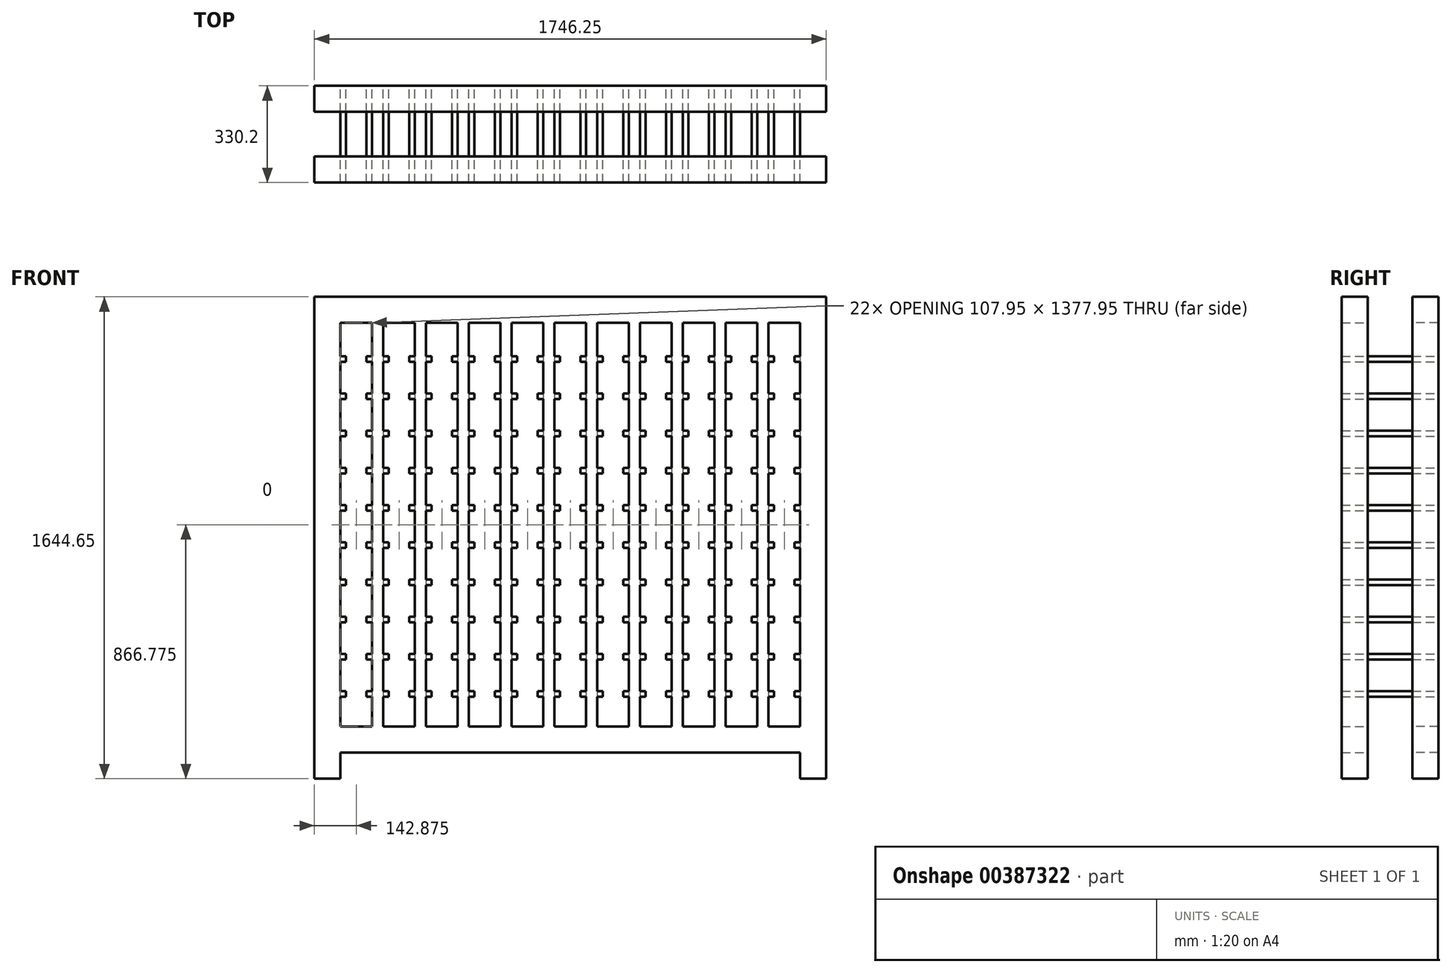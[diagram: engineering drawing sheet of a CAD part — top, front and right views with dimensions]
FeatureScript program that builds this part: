
annotation { "Feature Type Name" : "Feature", "Feature Type Description" : "" }
export const myFeature = defineFeature(function(context is Context, id is Id, definition is map)
    precondition{}
    {
        {
            var Q0;
            Q0=qCreatedBy(makeId("Front.planeOp"),FACE);
            var sketch = newSketch(context, id + "F0", { "sketchPlane" : qUnion([Q0])});
            skLineSegment(sketch, "E0.bottom", {"start": v(0, 0) * mm, "end": v(88.9, 0) * mm});
            skLineSegment(sketch, "E0.top", {"start": v(0, 1644.65) * mm, "end": v(88.9, 1644.65) * mm});
            skLineSegment(sketch, "E0.left", {"start": v(0, 0) * mm, "end": v(0, 1644.65) * mm});
            skLineSegment(sketch, "E0.right", {"start": v(88.9, 0) * mm, "end": v(88.9, 1644.65) * mm});
            skLineSegment(sketch, "E1.bottom", {"start": v(88.9, 1644.65) * mm, "end": v(1657.35, 1644.65) * mm});
            skLineSegment(sketch, "E1.top", {"start": v(88.9, 1555.75) * mm, "end": v(1657.35, 1555.75) * mm});
            skLineSegment(sketch, "E1.left", {"start": v(88.9, 1644.65) * mm, "end": v(88.9, 1555.75) * mm});
            skLineSegment(sketch, "E1.right", {"start": v(1657.35, 1644.65) * mm, "end": v(1657.35, 1555.75) * mm});
            skLineSegment(sketch, "E2.bottom", {"start": v(88.9, 177.8) * mm, "end": v(1657.35, 177.8) * mm});
            skLineSegment(sketch, "E2.top", {"start": v(88.9, 88.9) * mm, "end": v(1657.35, 88.9) * mm});
            skLineSegment(sketch, "E2.left", {"start": v(88.9, 177.8) * mm, "end": v(88.9, 88.9) * mm});
            skLineSegment(sketch, "E2.right", {"start": v(1657.35, 177.8) * mm, "end": v(1657.35, 88.9) * mm});
            skLineSegment(sketch, "E3.bottom", {"start": v(1657.35, 1644.65) * mm, "end": v(1746.25, 1644.65) * mm});
            skLineSegment(sketch, "E3.top", {"start": v(1657.35, 0) * mm, "end": v(1746.25, 0) * mm});
            skLineSegment(sketch, "E3.left", {"start": v(1657.35, 1644.65) * mm, "end": v(1657.35, 0) * mm});
            skLineSegment(sketch, "E3.right", {"start": v(1746.25, 1644.65) * mm, "end": v(1746.25, 0) * mm});
            skSolve(sketch);
        }
        {
            var Q0;
            Q0 = qSketchRegion(id + "F0", true);
            extrude(context, id + "F1", {"entities" : qUnion([Q0]), "depth" : 88.9 * mm});
        }
        {
            var Q0;
            Q0=makeQuery(id+"F1.opExtrude","CAP_FACE",FACE,{"disambiguationData":[OSD([sQuery(id+"F0.wireOp",EDGE,"E0.bottom"),sQuery(id+"F0.wireOp",EDGE,"E0.top"),sQuery(id+"F0.wireOp",EDGE,"E0.left"),sQuery(id+"F0.wireOp",EDGE,"E0.right"),sQuery(id+"F0.wireOp",EDGE,"E1.bottom"),sQuery(id+"F0.wireOp",EDGE,"E1.top"),sQuery(id+"F0.wireOp",EDGE,"E2.bottom"),sQuery(id+"F0.wireOp",EDGE,"E2.top"),sQuery(id+"F0.wireOp",EDGE,"E3.bottom"),sQuery(id+"F0.wireOp",EDGE,"E3.top"),sQuery(id+"F0.wireOp",EDGE,"E3.left"),sQuery(id+"F0.wireOp",EDGE,"E3.right")])],"isStart":false});
            var sketch = newSketch(context, id + "F2", { "sketchPlane" : qUnion([Q0])});
            skLineSegment(sketch, "E4.bottom", {"start": v(196.85, 1555.75) * mm, "end": v(234.95, 1555.75) * mm});
            skLineSegment(sketch, "E4.top", {"start": v(196.85, 177.8) * mm, "end": v(234.95, 177.8) * mm});
            skLineSegment(sketch, "E4.left", {"start": v(196.85, 1555.75) * mm, "end": v(196.85, 177.8) * mm});
            skLineSegment(sketch, "E4.right", {"start": v(234.95, 1555.75) * mm, "end": v(234.95, 177.8) * mm});
            skLineSegment(sketch, "E5.1.0.0", {"start": v(342.9, 1555.75) * mm, "end": v(342.9, 177.8) * mm});
            skLineSegment(sketch, "E5.1.0.1", {"start": v(381, 1555.75) * mm, "end": v(381, 177.8) * mm});
            skLineSegment(sketch, "E5.2.0.0", {"start": v(488.95, 1555.75) * mm, "end": v(488.95, 177.8) * mm});
            skLineSegment(sketch, "E5.2.0.1", {"start": v(527.05, 1555.75) * mm, "end": v(527.05, 177.8) * mm});
            skLineSegment(sketch, "E5.3.0.0", {"start": v(635, 1555.75) * mm, "end": v(635, 177.8) * mm});
            skLineSegment(sketch, "E5.3.0.1", {"start": v(673.1, 1555.75) * mm, "end": v(673.1, 177.8) * mm});
            skLineSegment(sketch, "E5.4.0.0", {"start": v(781.05, 1555.75) * mm, "end": v(781.05, 177.8) * mm});
            skLineSegment(sketch, "E5.4.0.1", {"start": v(819.15, 1555.75) * mm, "end": v(819.15, 177.8) * mm});
            skLineSegment(sketch, "E5.5.0.0", {"start": v(927.1, 1555.75) * mm, "end": v(927.1, 177.8) * mm});
            skLineSegment(sketch, "E5.5.0.1", {"start": v(965.2, 1555.75) * mm, "end": v(965.2, 177.8) * mm});
            skLineSegment(sketch, "E5.6.0.0", {"start": v(1073.15, 1555.75) * mm, "end": v(1073.15, 177.8) * mm});
            skLineSegment(sketch, "E5.6.0.1", {"start": v(1111.25, 1555.75) * mm, "end": v(1111.25, 177.8) * mm});
            skLineSegment(sketch, "E5.7.0.0", {"start": v(1219.2, 1555.75) * mm, "end": v(1219.2, 177.8) * mm});
            skLineSegment(sketch, "E5.7.0.1", {"start": v(1257.3, 1555.75) * mm, "end": v(1257.3, 177.8) * mm});
            skLineSegment(sketch, "E5.8.0.0", {"start": v(1365.25, 1555.75) * mm, "end": v(1365.25, 177.8) * mm});
            skLineSegment(sketch, "E5.8.0.1", {"start": v(1403.35, 1555.75) * mm, "end": v(1403.35, 177.8) * mm});
            skLineSegment(sketch, "E5.9.0.0", {"start": v(1511.3, 1555.75) * mm, "end": v(1511.3, 177.8) * mm});
            skLineSegment(sketch, "E5.9.0.1", {"start": v(1549.4, 1555.75) * mm, "end": v(1549.4, 177.8) * mm});
            skLineSegment(sketch, "E5.10.0.0", {"start": v(1657.35, 1555.75) * mm, "end": v(1657.35, 177.8) * mm});
            skLineSegment(sketch, "E5.10.0.1", {"start": v(1695.45, 1555.75) * mm, "end": v(1695.45, 177.8) * mm});
            skLineSegment(sketch, "E5.direction1", {"start": v(196.85, 177.8) * mm, "end": v(342.9, 177.8) * mm, "construction": true});
            skSolve(sketch);
        }
        {
            var Q0;
            Q0 = qSketchRegion(id + "F2", true);
            var Q1;
            {var subQ0=sQuery(id+"F2.wireOp",EDGE,"E5.1.0.0");Q1=makeQuery(id+"F2.imprint","IMPRINT",FACE,{"disambiguationData":[TD([[makeQuery(id+"F2.imprint","IMPRINT",EDGE,{"derivedFrom":subQ0}),1.0]])]});}
            var Q2;
            {var subQ0=sQuery(id+"F2.wireOp",EDGE,"E5.2.0.0");Q2=makeQuery(id+"F2.imprint","IMPRINT",FACE,{"disambiguationData":[TD([[makeQuery(id+"F2.imprint","IMPRINT",EDGE,{"derivedFrom":subQ0}),1.0]])]});}
            var Q3;
            {var subQ0=sQuery(id+"F2.wireOp",EDGE,"E5.3.0.0");Q3=makeQuery(id+"F2.imprint","IMPRINT",FACE,{"disambiguationData":[TD([[makeQuery(id+"F2.imprint","IMPRINT",EDGE,{"derivedFrom":subQ0}),1.0]])]});}
            var Q4;
            {var subQ0=sQuery(id+"F2.wireOp",EDGE,"E5.4.0.0");Q4=makeQuery(id+"F2.imprint","IMPRINT",FACE,{"disambiguationData":[TD([[makeQuery(id+"F2.imprint","IMPRINT",EDGE,{"derivedFrom":subQ0}),1.0]])]});}
            var Q5;
            {var subQ0=sQuery(id+"F2.wireOp",EDGE,"E5.5.0.0");Q5=makeQuery(id+"F2.imprint","IMPRINT",FACE,{"disambiguationData":[TD([[makeQuery(id+"F2.imprint","IMPRINT",EDGE,{"derivedFrom":subQ0}),1.0]])]});}
            var Q6;
            {var subQ0=sQuery(id+"F2.wireOp",EDGE,"E5.6.0.0");Q6=makeQuery(id+"F2.imprint","IMPRINT",FACE,{"disambiguationData":[TD([[makeQuery(id+"F2.imprint","IMPRINT",EDGE,{"derivedFrom":subQ0}),1.0]])]});}
            var Q7;
            {var subQ0=sQuery(id+"F2.wireOp",EDGE,"E5.7.0.0");Q7=makeQuery(id+"F2.imprint","IMPRINT",FACE,{"disambiguationData":[TD([[makeQuery(id+"F2.imprint","IMPRINT",EDGE,{"derivedFrom":subQ0}),1.0]])]});}
            var Q8;
            {var subQ0=sQuery(id+"F2.wireOp",EDGE,"E5.8.0.0");Q8=makeQuery(id+"F2.imprint","IMPRINT",FACE,{"disambiguationData":[TD([[makeQuery(id+"F2.imprint","IMPRINT",EDGE,{"derivedFrom":subQ0}),1.0]])]});}
            var Q9;
            {var subQ0=sQuery(id+"F2.wireOp",EDGE,"E5.9.0.0");Q9=makeQuery(id+"F2.imprint","IMPRINT",FACE,{"disambiguationData":[TD([[makeQuery(id+"F2.imprint","IMPRINT",EDGE,{"derivedFrom":subQ0}),1.0]])]});}
            var Q10;
            {var subQ0=sQuery(id+"F2.wireOp",EDGE,"E5.10.0.0");Q10=makeQuery(id+"F2.imprint","IMPRINT",FACE,{"disambiguationData":[TD([[makeQuery(id+"F2.imprint","IMPRINT",EDGE,{"derivedFrom":subQ0}),1.0]])]});}
            extrude(context, id + "F3", {"entities" : qUnion([Q0, Q1, Q2, Q3, Q4, Q5, Q6, Q7, Q8, Q9, Q10]), "operationType" : NewBodyOperationType.ADD, "oppositeDirection" : true, "depth" : 88.9 * mm});
        }
        {
            var Q0;
            {var subQ0=sQuery(id+"F0.wireOp",EDGE,"E3.right");var subQ1=sQuery(id+"F0.wireOp",EDGE,"E3.left");var subQ2=sQuery(id+"F0.wireOp",EDGE,"E3.top");var subQ3=sQuery(id+"F0.wireOp",EDGE,"E3.bottom");var subQ4=sQuery(id+"F0.wireOp",EDGE,"E2.top");var subQ5=sQuery(id+"F0.wireOp",EDGE,"E2.bottom");var subQ6=sQuery(id+"F0.wireOp",EDGE,"E1.top");var subQ7=sQuery(id+"F0.wireOp",EDGE,"E1.bottom");var subQ8=sQuery(id+"F0.wireOp",EDGE,"E0.right");var subQ9=sQuery(id+"F0.wireOp",EDGE,"E0.left");var subQ10=sQuery(id+"F0.wireOp",EDGE,"E0.top");var subQ11=sQuery(id+"F0.wireOp",EDGE,"E0.bottom");Q0=makeQuery(id+"F3.boolean.opBoolean","MERGE",FACE,{"derivedFrom":[makeQuery(id+"F1.opExtrude","CAP_FACE",FACE,{"disambiguationData":[OSD([subQ11,subQ10,subQ9,subQ8,subQ7,subQ6,subQ5,subQ4,subQ3,subQ2,subQ1,subQ0])],"isStart":false}),makeQuery(id+"F3.opExtrude","CAP_FACE",FACE,{"disambiguationData":[OSD([subQ11,subQ10,subQ9,subQ8,subQ7,subQ6,subQ5,subQ4,subQ3,subQ2,subQ1,subQ0,sQuery(id+"F2.wireOp",EDGE,"E4.left"),sQuery(id+"F2.wireOp",EDGE,"E4.right"),sQuery(id+"F2.wireOp",EDGE,"E5.1.0.0"),sQuery(id+"F2.wireOp",EDGE,"E5.1.0.1"),sQuery(id+"F2.wireOp",EDGE,"E5.2.0.0"),sQuery(id+"F2.wireOp",EDGE,"E5.2.0.1"),sQuery(id+"F2.wireOp",EDGE,"E5.3.0.0"),sQuery(id+"F2.wireOp",EDGE,"E5.3.0.1"),sQuery(id+"F2.wireOp",EDGE,"E5.4.0.0"),sQuery(id+"F2.wireOp",EDGE,"E5.4.0.1"),sQuery(id+"F2.wireOp",EDGE,"E5.5.0.0"),sQuery(id+"F2.wireOp",EDGE,"E5.5.0.1"),sQuery(id+"F2.wireOp",EDGE,"E5.6.0.0"),sQuery(id+"F2.wireOp",EDGE,"E5.6.0.1"),sQuery(id+"F2.wireOp",EDGE,"E5.7.0.0"),sQuery(id+"F2.wireOp",EDGE,"E5.7.0.1"),sQuery(id+"F2.wireOp",EDGE,"E5.8.0.0"),sQuery(id+"F2.wireOp",EDGE,"E5.8.0.1"),sQuery(id+"F2.wireOp",EDGE,"E5.9.0.0"),sQuery(id+"F2.wireOp",EDGE,"E5.9.0.1"),sQuery(id+"F2.wireOp",EDGE,"E5.10.0.0")])],"isStart":true})]});}
            cPlane(context, id + "F4", {"entities" : qUnion([Q0]), "cplaneType" : CPlaneType.OFFSET, "offset" : 165.1 * mm, "oppositeDirection" : true, "width" : 152.4 * mm, "height" : 152.4 * mm});
        }
        {
            var Q0;
            Q0=makeQuery(id+"F1.opExtrude","SWEPT_BODY",BODY,{"disambiguationData":[OSD([sQuery(id+"F0.wireOp",EDGE,"E0.bottom"),sQuery(id+"F0.wireOp",EDGE,"E0.top"),sQuery(id+"F0.wireOp",EDGE,"E0.left"),sQuery(id+"F0.wireOp",EDGE,"E0.right"),sQuery(id+"F0.wireOp",EDGE,"E1.bottom"),sQuery(id+"F0.wireOp",EDGE,"E1.top"),sQuery(id+"F0.wireOp",EDGE,"E2.bottom"),sQuery(id+"F0.wireOp",EDGE,"E2.top"),sQuery(id+"F0.wireOp",EDGE,"E3.bottom"),sQuery(id+"F0.wireOp",EDGE,"E3.top"),sQuery(id+"F0.wireOp",EDGE,"E3.left"),sQuery(id+"F0.wireOp",EDGE,"E3.right")])]});
            var Q1;
            Q1=qCreatedBy(id+"F4.planeOp",FACE);
            mirror(context, id + "F5", {"entities" : qUnion([Q0]), "mirrorPlane" : qUnion([Q1])});
        }
        {
            var Q0;
            Q0=qCreatedBy(id+"F4.planeOp",FACE);
            var sketch = newSketch(context, id + "F6", { "sketchPlane" : qUnion([Q0])});
            skLineSegment(sketch, "E6.bottom", {"start": v(88.9, 298.45) * mm, "end": v(107.95, 298.45) * mm});
            skLineSegment(sketch, "E6.top", {"start": v(88.9, 279.4) * mm, "end": v(107.95, 279.4) * mm});
            skLineSegment(sketch, "E6.left", {"start": v(88.9, 298.45) * mm, "end": v(88.9, 279.4) * mm});
            skLineSegment(sketch, "E6.right", {"start": v(107.95, 298.45) * mm, "end": v(107.95, 279.4) * mm});
            skLineSegment(sketch, "E7.0.1.0", {"start": v(107.95, 425.45) * mm, "end": v(107.95, 406.4) * mm});
            skLineSegment(sketch, "E7.0.1.1", {"start": v(88.9, 425.45) * mm, "end": v(88.9, 406.4) * mm});
            skLineSegment(sketch, "E7.0.1.2", {"start": v(88.9, 406.4) * mm, "end": v(107.95, 406.4) * mm});
            skLineSegment(sketch, "E7.0.1.3", {"start": v(88.9, 425.45) * mm, "end": v(107.95, 425.45) * mm});
            skLineSegment(sketch, "E7.0.2.0", {"start": v(107.95, 552.45) * mm, "end": v(107.95, 533.4) * mm});
            skLineSegment(sketch, "E7.0.2.1", {"start": v(88.9, 552.45) * mm, "end": v(88.9, 533.4) * mm});
            skLineSegment(sketch, "E7.0.2.2", {"start": v(88.9, 533.4) * mm, "end": v(107.95, 533.4) * mm});
            skLineSegment(sketch, "E7.0.2.3", {"start": v(88.9, 552.45) * mm, "end": v(107.95, 552.45) * mm});
            skLineSegment(sketch, "E7.0.3.0", {"start": v(107.95, 679.45) * mm, "end": v(107.95, 660.4) * mm});
            skLineSegment(sketch, "E7.0.3.1", {"start": v(88.9, 679.45) * mm, "end": v(88.9, 660.4) * mm});
            skLineSegment(sketch, "E7.0.3.2", {"start": v(88.9, 660.4) * mm, "end": v(107.95, 660.4) * mm});
            skLineSegment(sketch, "E7.0.3.3", {"start": v(88.9, 679.45) * mm, "end": v(107.95, 679.45) * mm});
            skLineSegment(sketch, "E7.0.4.0", {"start": v(107.95, 806.45) * mm, "end": v(107.95, 787.4) * mm});
            skLineSegment(sketch, "E7.0.4.1", {"start": v(88.9, 806.45) * mm, "end": v(88.9, 787.4) * mm});
            skLineSegment(sketch, "E7.0.4.2", {"start": v(88.9, 787.4) * mm, "end": v(107.95, 787.4) * mm});
            skLineSegment(sketch, "E7.0.4.3", {"start": v(88.9, 806.45) * mm, "end": v(107.95, 806.45) * mm});
            skLineSegment(sketch, "E7.0.5.0", {"start": v(107.95, 933.45) * mm, "end": v(107.95, 914.4) * mm});
            skLineSegment(sketch, "E7.0.5.1", {"start": v(88.9, 933.45) * mm, "end": v(88.9, 914.4) * mm});
            skLineSegment(sketch, "E7.0.5.2", {"start": v(88.9, 914.4) * mm, "end": v(107.95, 914.4) * mm});
            skLineSegment(sketch, "E7.0.5.3", {"start": v(88.9, 933.45) * mm, "end": v(107.95, 933.45) * mm});
            skLineSegment(sketch, "E7.0.6.0", {"start": v(107.95, 1060.45) * mm, "end": v(107.95, 1041.4) * mm});
            skLineSegment(sketch, "E7.0.6.1", {"start": v(88.9, 1060.45) * mm, "end": v(88.9, 1041.4) * mm});
            skLineSegment(sketch, "E7.0.6.2", {"start": v(88.9, 1041.4) * mm, "end": v(107.95, 1041.4) * mm});
            skLineSegment(sketch, "E7.0.6.3", {"start": v(88.9, 1060.45) * mm, "end": v(107.95, 1060.45) * mm});
            skLineSegment(sketch, "E7.0.7.0", {"start": v(107.95, 1187.45) * mm, "end": v(107.95, 1168.4) * mm});
            skLineSegment(sketch, "E7.0.7.1", {"start": v(88.9, 1187.45) * mm, "end": v(88.9, 1168.4) * mm});
            skLineSegment(sketch, "E7.0.7.2", {"start": v(88.9, 1168.4) * mm, "end": v(107.95, 1168.4) * mm});
            skLineSegment(sketch, "E7.0.7.3", {"start": v(88.9, 1187.45) * mm, "end": v(107.95, 1187.45) * mm});
            skLineSegment(sketch, "E7.0.8.0", {"start": v(107.95, 1314.45) * mm, "end": v(107.95, 1295.4) * mm});
            skLineSegment(sketch, "E7.0.8.1", {"start": v(88.9, 1314.45) * mm, "end": v(88.9, 1295.4) * mm});
            skLineSegment(sketch, "E7.0.8.2", {"start": v(88.9, 1295.4) * mm, "end": v(107.95, 1295.4) * mm});
            skLineSegment(sketch, "E7.0.8.3", {"start": v(88.9, 1314.45) * mm, "end": v(107.95, 1314.45) * mm});
            skLineSegment(sketch, "E7.1.0.0", {"start": v(254, 298.45) * mm, "end": v(254, 279.4) * mm});
            skLineSegment(sketch, "E7.1.0.1", {"start": v(234.95, 298.45) * mm, "end": v(234.95, 279.4) * mm});
            skLineSegment(sketch, "E7.1.0.2", {"start": v(234.95, 279.4) * mm, "end": v(254, 279.4) * mm});
            skLineSegment(sketch, "E7.1.0.3", {"start": v(234.95, 298.45) * mm, "end": v(254, 298.45) * mm});
            skLineSegment(sketch, "E7.1.1.0", {"start": v(254, 425.45) * mm, "end": v(254, 406.4) * mm});
            skLineSegment(sketch, "E7.1.1.1", {"start": v(234.95, 425.45) * mm, "end": v(234.95, 406.4) * mm});
            skLineSegment(sketch, "E7.1.1.2", {"start": v(234.95, 406.4) * mm, "end": v(254, 406.4) * mm});
            skLineSegment(sketch, "E7.1.1.3", {"start": v(234.95, 425.45) * mm, "end": v(254, 425.45) * mm});
            skLineSegment(sketch, "E7.1.2.0", {"start": v(254, 552.45) * mm, "end": v(254, 533.4) * mm});
            skLineSegment(sketch, "E7.1.2.1", {"start": v(234.95, 552.45) * mm, "end": v(234.95, 533.4) * mm});
            skLineSegment(sketch, "E7.1.2.2", {"start": v(234.95, 533.4) * mm, "end": v(254, 533.4) * mm});
            skLineSegment(sketch, "E7.1.2.3", {"start": v(234.95, 552.45) * mm, "end": v(254, 552.45) * mm});
            skLineSegment(sketch, "E7.1.3.0", {"start": v(254, 679.45) * mm, "end": v(254, 660.4) * mm});
            skLineSegment(sketch, "E7.1.3.1", {"start": v(234.95, 679.45) * mm, "end": v(234.95, 660.4) * mm});
            skLineSegment(sketch, "E7.1.3.2", {"start": v(234.95, 660.4) * mm, "end": v(254, 660.4) * mm});
            skLineSegment(sketch, "E7.1.3.3", {"start": v(234.95, 679.45) * mm, "end": v(254, 679.45) * mm});
            skLineSegment(sketch, "E7.1.4.0", {"start": v(254, 806.45) * mm, "end": v(254, 787.4) * mm});
            skLineSegment(sketch, "E7.1.4.1", {"start": v(234.95, 806.45) * mm, "end": v(234.95, 787.4) * mm});
            skLineSegment(sketch, "E7.1.4.2", {"start": v(234.95, 787.4) * mm, "end": v(254, 787.4) * mm});
            skLineSegment(sketch, "E7.1.4.3", {"start": v(234.95, 806.45) * mm, "end": v(254, 806.45) * mm});
            skLineSegment(sketch, "E7.1.5.0", {"start": v(254, 933.45) * mm, "end": v(254, 914.4) * mm});
            skLineSegment(sketch, "E7.1.5.1", {"start": v(234.95, 933.45) * mm, "end": v(234.95, 914.4) * mm});
            skLineSegment(sketch, "E7.1.5.2", {"start": v(234.95, 914.4) * mm, "end": v(254, 914.4) * mm});
            skLineSegment(sketch, "E7.1.5.3", {"start": v(234.95, 933.45) * mm, "end": v(254, 933.45) * mm});
            skLineSegment(sketch, "E7.1.6.0", {"start": v(254, 1060.45) * mm, "end": v(254, 1041.4) * mm});
            skLineSegment(sketch, "E7.1.6.1", {"start": v(234.95, 1060.45) * mm, "end": v(234.95, 1041.4) * mm});
            skLineSegment(sketch, "E7.1.6.2", {"start": v(234.95, 1041.4) * mm, "end": v(254, 1041.4) * mm});
            skLineSegment(sketch, "E7.1.6.3", {"start": v(234.95, 1060.45) * mm, "end": v(254, 1060.45) * mm});
            skLineSegment(sketch, "E7.1.7.0", {"start": v(254, 1187.45) * mm, "end": v(254, 1168.4) * mm});
            skLineSegment(sketch, "E7.1.7.1", {"start": v(234.95, 1187.45) * mm, "end": v(234.95, 1168.4) * mm});
            skLineSegment(sketch, "E7.1.7.2", {"start": v(234.95, 1168.4) * mm, "end": v(254, 1168.4) * mm});
            skLineSegment(sketch, "E7.1.7.3", {"start": v(234.95, 1187.45) * mm, "end": v(254, 1187.45) * mm});
            skLineSegment(sketch, "E7.1.8.0", {"start": v(254, 1314.45) * mm, "end": v(254, 1295.4) * mm});
            skLineSegment(sketch, "E7.1.8.1", {"start": v(234.95, 1314.45) * mm, "end": v(234.95, 1295.4) * mm});
            skLineSegment(sketch, "E7.1.8.2", {"start": v(234.95, 1295.4) * mm, "end": v(254, 1295.4) * mm});
            skLineSegment(sketch, "E7.1.8.3", {"start": v(234.95, 1314.45) * mm, "end": v(254, 1314.45) * mm});
            skLineSegment(sketch, "E7.2.0.0", {"start": v(400.05, 298.45) * mm, "end": v(400.05, 279.4) * mm});
            skLineSegment(sketch, "E7.2.0.1", {"start": v(381, 298.45) * mm, "end": v(381, 279.4) * mm});
            skLineSegment(sketch, "E7.2.0.2", {"start": v(381, 279.4) * mm, "end": v(400.05, 279.4) * mm});
            skLineSegment(sketch, "E7.2.0.3", {"start": v(381, 298.45) * mm, "end": v(400.05, 298.45) * mm});
            skLineSegment(sketch, "E7.2.1.0", {"start": v(400.05, 425.45) * mm, "end": v(400.05, 406.4) * mm});
            skLineSegment(sketch, "E7.2.1.1", {"start": v(381, 425.45) * mm, "end": v(381, 406.4) * mm});
            skLineSegment(sketch, "E7.2.1.2", {"start": v(381, 406.4) * mm, "end": v(400.05, 406.4) * mm});
            skLineSegment(sketch, "E7.2.1.3", {"start": v(381, 425.45) * mm, "end": v(400.05, 425.45) * mm});
            skLineSegment(sketch, "E7.2.2.0", {"start": v(400.05, 552.45) * mm, "end": v(400.05, 533.4) * mm});
            skLineSegment(sketch, "E7.2.2.1", {"start": v(381, 552.45) * mm, "end": v(381, 533.4) * mm});
            skLineSegment(sketch, "E7.2.2.2", {"start": v(381, 533.4) * mm, "end": v(400.05, 533.4) * mm});
            skLineSegment(sketch, "E7.2.2.3", {"start": v(381, 552.45) * mm, "end": v(400.05, 552.45) * mm});
            skLineSegment(sketch, "E7.2.3.0", {"start": v(400.05, 679.45) * mm, "end": v(400.05, 660.4) * mm});
            skLineSegment(sketch, "E7.2.3.1", {"start": v(381, 679.45) * mm, "end": v(381, 660.4) * mm});
            skLineSegment(sketch, "E7.2.3.2", {"start": v(381, 660.4) * mm, "end": v(400.05, 660.4) * mm});
            skLineSegment(sketch, "E7.2.3.3", {"start": v(381, 679.45) * mm, "end": v(400.05, 679.45) * mm});
            skLineSegment(sketch, "E7.2.4.0", {"start": v(400.05, 806.45) * mm, "end": v(400.05, 787.4) * mm});
            skLineSegment(sketch, "E7.2.4.1", {"start": v(381, 806.45) * mm, "end": v(381, 787.4) * mm});
            skLineSegment(sketch, "E7.2.4.2", {"start": v(381, 787.4) * mm, "end": v(400.05, 787.4) * mm});
            skLineSegment(sketch, "E7.2.4.3", {"start": v(381, 806.45) * mm, "end": v(400.05, 806.45) * mm});
            skLineSegment(sketch, "E7.2.5.0", {"start": v(400.05, 933.45) * mm, "end": v(400.05, 914.4) * mm});
            skLineSegment(sketch, "E7.2.5.1", {"start": v(381, 933.45) * mm, "end": v(381, 914.4) * mm});
            skLineSegment(sketch, "E7.2.5.2", {"start": v(381, 914.4) * mm, "end": v(400.05, 914.4) * mm});
            skLineSegment(sketch, "E7.2.5.3", {"start": v(381, 933.45) * mm, "end": v(400.05, 933.45) * mm});
            skLineSegment(sketch, "E7.2.6.0", {"start": v(400.05, 1060.45) * mm, "end": v(400.05, 1041.4) * mm});
            skLineSegment(sketch, "E7.2.6.1", {"start": v(381, 1060.45) * mm, "end": v(381, 1041.4) * mm});
            skLineSegment(sketch, "E7.2.6.2", {"start": v(381, 1041.4) * mm, "end": v(400.05, 1041.4) * mm});
            skLineSegment(sketch, "E7.2.6.3", {"start": v(381, 1060.45) * mm, "end": v(400.05, 1060.45) * mm});
            skLineSegment(sketch, "E7.2.7.0", {"start": v(400.05, 1187.45) * mm, "end": v(400.05, 1168.4) * mm});
            skLineSegment(sketch, "E7.2.7.1", {"start": v(381, 1187.45) * mm, "end": v(381, 1168.4) * mm});
            skLineSegment(sketch, "E7.2.7.2", {"start": v(381, 1168.4) * mm, "end": v(400.05, 1168.4) * mm});
            skLineSegment(sketch, "E7.2.7.3", {"start": v(381, 1187.45) * mm, "end": v(400.05, 1187.45) * mm});
            skLineSegment(sketch, "E7.2.8.0", {"start": v(400.05, 1314.45) * mm, "end": v(400.05, 1295.4) * mm});
            skLineSegment(sketch, "E7.2.8.1", {"start": v(381, 1314.45) * mm, "end": v(381, 1295.4) * mm});
            skLineSegment(sketch, "E7.2.8.2", {"start": v(381, 1295.4) * mm, "end": v(400.05, 1295.4) * mm});
            skLineSegment(sketch, "E7.2.8.3", {"start": v(381, 1314.45) * mm, "end": v(400.05, 1314.45) * mm});
            skLineSegment(sketch, "E7.3.0.0", {"start": v(546.1, 298.45) * mm, "end": v(546.1, 279.4) * mm});
            skLineSegment(sketch, "E7.3.0.1", {"start": v(527.05, 298.45) * mm, "end": v(527.05, 279.4) * mm});
            skLineSegment(sketch, "E7.3.0.2", {"start": v(527.05, 279.4) * mm, "end": v(546.1, 279.4) * mm});
            skLineSegment(sketch, "E7.3.0.3", {"start": v(527.05, 298.45) * mm, "end": v(546.1, 298.45) * mm});
            skLineSegment(sketch, "E7.3.1.0", {"start": v(546.1, 425.45) * mm, "end": v(546.1, 406.4) * mm});
            skLineSegment(sketch, "E7.3.1.1", {"start": v(527.05, 425.45) * mm, "end": v(527.05, 406.4) * mm});
            skLineSegment(sketch, "E7.3.1.2", {"start": v(527.05, 406.4) * mm, "end": v(546.1, 406.4) * mm});
            skLineSegment(sketch, "E7.3.1.3", {"start": v(527.05, 425.45) * mm, "end": v(546.1, 425.45) * mm});
            skLineSegment(sketch, "E7.3.2.0", {"start": v(546.1, 552.45) * mm, "end": v(546.1, 533.4) * mm});
            skLineSegment(sketch, "E7.3.2.1", {"start": v(527.05, 552.45) * mm, "end": v(527.05, 533.4) * mm});
            skLineSegment(sketch, "E7.3.2.2", {"start": v(527.05, 533.4) * mm, "end": v(546.1, 533.4) * mm});
            skLineSegment(sketch, "E7.3.2.3", {"start": v(527.05, 552.45) * mm, "end": v(546.1, 552.45) * mm});
            skLineSegment(sketch, "E7.3.3.0", {"start": v(546.1, 679.45) * mm, "end": v(546.1, 660.4) * mm});
            skLineSegment(sketch, "E7.3.3.1", {"start": v(527.05, 679.45) * mm, "end": v(527.05, 660.4) * mm});
            skLineSegment(sketch, "E7.3.3.2", {"start": v(527.05, 660.4) * mm, "end": v(546.1, 660.4) * mm});
            skLineSegment(sketch, "E7.3.3.3", {"start": v(527.05, 679.45) * mm, "end": v(546.1, 679.45) * mm});
            skLineSegment(sketch, "E7.3.4.0", {"start": v(546.1, 806.45) * mm, "end": v(546.1, 787.4) * mm});
            skLineSegment(sketch, "E7.3.4.1", {"start": v(527.05, 806.45) * mm, "end": v(527.05, 787.4) * mm});
            skLineSegment(sketch, "E7.3.4.2", {"start": v(527.05, 787.4) * mm, "end": v(546.1, 787.4) * mm});
            skLineSegment(sketch, "E7.3.4.3", {"start": v(527.05, 806.45) * mm, "end": v(546.1, 806.45) * mm});
            skLineSegment(sketch, "E7.3.5.0", {"start": v(546.1, 933.45) * mm, "end": v(546.1, 914.4) * mm});
            skLineSegment(sketch, "E7.3.5.1", {"start": v(527.05, 933.45) * mm, "end": v(527.05, 914.4) * mm});
            skLineSegment(sketch, "E7.3.5.2", {"start": v(527.05, 914.4) * mm, "end": v(546.1, 914.4) * mm});
            skLineSegment(sketch, "E7.3.5.3", {"start": v(527.05, 933.45) * mm, "end": v(546.1, 933.45) * mm});
            skLineSegment(sketch, "E7.3.6.0", {"start": v(546.1, 1060.45) * mm, "end": v(546.1, 1041.4) * mm});
            skLineSegment(sketch, "E7.3.6.1", {"start": v(527.05, 1060.45) * mm, "end": v(527.05, 1041.4) * mm});
            skLineSegment(sketch, "E7.3.6.2", {"start": v(527.05, 1041.4) * mm, "end": v(546.1, 1041.4) * mm});
            skLineSegment(sketch, "E7.3.6.3", {"start": v(527.05, 1060.45) * mm, "end": v(546.1, 1060.45) * mm});
            skLineSegment(sketch, "E7.3.7.0", {"start": v(546.1, 1187.45) * mm, "end": v(546.1, 1168.4) * mm});
            skLineSegment(sketch, "E7.3.7.1", {"start": v(527.05, 1187.45) * mm, "end": v(527.05, 1168.4) * mm});
            skLineSegment(sketch, "E7.3.7.2", {"start": v(527.05, 1168.4) * mm, "end": v(546.1, 1168.4) * mm});
            skLineSegment(sketch, "E7.3.7.3", {"start": v(527.05, 1187.45) * mm, "end": v(546.1, 1187.45) * mm});
            skLineSegment(sketch, "E7.3.8.0", {"start": v(546.1, 1314.45) * mm, "end": v(546.1, 1295.4) * mm});
            skLineSegment(sketch, "E7.3.8.1", {"start": v(527.05, 1314.45) * mm, "end": v(527.05, 1295.4) * mm});
            skLineSegment(sketch, "E7.3.8.2", {"start": v(527.05, 1295.4) * mm, "end": v(546.1, 1295.4) * mm});
            skLineSegment(sketch, "E7.3.8.3", {"start": v(527.05, 1314.45) * mm, "end": v(546.1, 1314.45) * mm});
            skLineSegment(sketch, "E7.4.0.0", {"start": v(692.15, 298.45) * mm, "end": v(692.15, 279.4) * mm});
            skLineSegment(sketch, "E7.4.0.1", {"start": v(673.1, 298.45) * mm, "end": v(673.1, 279.4) * mm});
            skLineSegment(sketch, "E7.4.0.2", {"start": v(673.1, 279.4) * mm, "end": v(692.15, 279.4) * mm});
            skLineSegment(sketch, "E7.4.0.3", {"start": v(673.1, 298.45) * mm, "end": v(692.15, 298.45) * mm});
            skLineSegment(sketch, "E7.4.1.0", {"start": v(692.15, 425.45) * mm, "end": v(692.15, 406.4) * mm});
            skLineSegment(sketch, "E7.4.1.1", {"start": v(673.1, 425.45) * mm, "end": v(673.1, 406.4) * mm});
            skLineSegment(sketch, "E7.4.1.2", {"start": v(673.1, 406.4) * mm, "end": v(692.15, 406.4) * mm});
            skLineSegment(sketch, "E7.4.1.3", {"start": v(673.1, 425.45) * mm, "end": v(692.15, 425.45) * mm});
            skLineSegment(sketch, "E7.4.2.0", {"start": v(692.15, 552.45) * mm, "end": v(692.15, 533.4) * mm});
            skLineSegment(sketch, "E7.4.2.1", {"start": v(673.1, 552.45) * mm, "end": v(673.1, 533.4) * mm});
            skLineSegment(sketch, "E7.4.2.2", {"start": v(673.1, 533.4) * mm, "end": v(692.15, 533.4) * mm});
            skLineSegment(sketch, "E7.4.2.3", {"start": v(673.1, 552.45) * mm, "end": v(692.15, 552.45) * mm});
            skLineSegment(sketch, "E7.4.3.0", {"start": v(692.15, 679.45) * mm, "end": v(692.15, 660.4) * mm});
            skLineSegment(sketch, "E7.4.3.1", {"start": v(673.1, 679.45) * mm, "end": v(673.1, 660.4) * mm});
            skLineSegment(sketch, "E7.4.3.2", {"start": v(673.1, 660.4) * mm, "end": v(692.15, 660.4) * mm});
            skLineSegment(sketch, "E7.4.3.3", {"start": v(673.1, 679.45) * mm, "end": v(692.15, 679.45) * mm});
            skLineSegment(sketch, "E7.4.4.0", {"start": v(692.15, 806.45) * mm, "end": v(692.15, 787.4) * mm});
            skLineSegment(sketch, "E7.4.4.1", {"start": v(673.1, 806.45) * mm, "end": v(673.1, 787.4) * mm});
            skLineSegment(sketch, "E7.4.4.2", {"start": v(673.1, 787.4) * mm, "end": v(692.15, 787.4) * mm});
            skLineSegment(sketch, "E7.4.4.3", {"start": v(673.1, 806.45) * mm, "end": v(692.15, 806.45) * mm});
            skLineSegment(sketch, "E7.4.5.0", {"start": v(692.15, 933.45) * mm, "end": v(692.15, 914.4) * mm});
            skLineSegment(sketch, "E7.4.5.1", {"start": v(673.1, 933.45) * mm, "end": v(673.1, 914.4) * mm});
            skLineSegment(sketch, "E7.4.5.2", {"start": v(673.1, 914.4) * mm, "end": v(692.15, 914.4) * mm});
            skLineSegment(sketch, "E7.4.5.3", {"start": v(673.1, 933.45) * mm, "end": v(692.15, 933.45) * mm});
            skLineSegment(sketch, "E7.4.6.0", {"start": v(692.15, 1060.45) * mm, "end": v(692.15, 1041.4) * mm});
            skLineSegment(sketch, "E7.4.6.1", {"start": v(673.1, 1060.45) * mm, "end": v(673.1, 1041.4) * mm});
            skLineSegment(sketch, "E7.4.6.2", {"start": v(673.1, 1041.4) * mm, "end": v(692.15, 1041.4) * mm});
            skLineSegment(sketch, "E7.4.6.3", {"start": v(673.1, 1060.45) * mm, "end": v(692.15, 1060.45) * mm});
            skLineSegment(sketch, "E7.4.7.0", {"start": v(692.15, 1187.45) * mm, "end": v(692.15, 1168.4) * mm});
            skLineSegment(sketch, "E7.4.7.1", {"start": v(673.1, 1187.45) * mm, "end": v(673.1, 1168.4) * mm});
            skLineSegment(sketch, "E7.4.7.2", {"start": v(673.1, 1168.4) * mm, "end": v(692.15, 1168.4) * mm});
            skLineSegment(sketch, "E7.4.7.3", {"start": v(673.1, 1187.45) * mm, "end": v(692.15, 1187.45) * mm});
            skLineSegment(sketch, "E7.4.8.0", {"start": v(692.15, 1314.45) * mm, "end": v(692.15, 1295.4) * mm});
            skLineSegment(sketch, "E7.4.8.1", {"start": v(673.1, 1314.45) * mm, "end": v(673.1, 1295.4) * mm});
            skLineSegment(sketch, "E7.4.8.2", {"start": v(673.1, 1295.4) * mm, "end": v(692.15, 1295.4) * mm});
            skLineSegment(sketch, "E7.4.8.3", {"start": v(673.1, 1314.45) * mm, "end": v(692.15, 1314.45) * mm});
            skLineSegment(sketch, "E7.5.0.0", {"start": v(838.2, 298.45) * mm, "end": v(838.2, 279.4) * mm});
            skLineSegment(sketch, "E7.5.0.1", {"start": v(819.15, 298.45) * mm, "end": v(819.15, 279.4) * mm});
            skLineSegment(sketch, "E7.5.0.2", {"start": v(819.15, 279.4) * mm, "end": v(838.2, 279.4) * mm});
            skLineSegment(sketch, "E7.5.0.3", {"start": v(819.15, 298.45) * mm, "end": v(838.2, 298.45) * mm});
            skLineSegment(sketch, "E7.5.1.0", {"start": v(838.2, 425.45) * mm, "end": v(838.2, 406.4) * mm});
            skLineSegment(sketch, "E7.5.1.1", {"start": v(819.15, 425.45) * mm, "end": v(819.15, 406.4) * mm});
            skLineSegment(sketch, "E7.5.1.2", {"start": v(819.15, 406.4) * mm, "end": v(838.2, 406.4) * mm});
            skLineSegment(sketch, "E7.5.1.3", {"start": v(819.15, 425.45) * mm, "end": v(838.2, 425.45) * mm});
            skLineSegment(sketch, "E7.5.2.0", {"start": v(838.2, 552.45) * mm, "end": v(838.2, 533.4) * mm});
            skLineSegment(sketch, "E7.5.2.1", {"start": v(819.15, 552.45) * mm, "end": v(819.15, 533.4) * mm});
            skLineSegment(sketch, "E7.5.2.2", {"start": v(819.15, 533.4) * mm, "end": v(838.2, 533.4) * mm});
            skLineSegment(sketch, "E7.5.2.3", {"start": v(819.15, 552.45) * mm, "end": v(838.2, 552.45) * mm});
            skLineSegment(sketch, "E7.5.3.0", {"start": v(838.2, 679.45) * mm, "end": v(838.2, 660.4) * mm});
            skLineSegment(sketch, "E7.5.3.1", {"start": v(819.15, 679.45) * mm, "end": v(819.15, 660.4) * mm});
            skLineSegment(sketch, "E7.5.3.2", {"start": v(819.15, 660.4) * mm, "end": v(838.2, 660.4) * mm});
            skLineSegment(sketch, "E7.5.3.3", {"start": v(819.15, 679.45) * mm, "end": v(838.2, 679.45) * mm});
            skLineSegment(sketch, "E7.5.4.0", {"start": v(838.2, 806.45) * mm, "end": v(838.2, 787.4) * mm});
            skLineSegment(sketch, "E7.5.4.1", {"start": v(819.15, 806.45) * mm, "end": v(819.15, 787.4) * mm});
            skLineSegment(sketch, "E7.5.4.2", {"start": v(819.15, 787.4) * mm, "end": v(838.2, 787.4) * mm});
            skLineSegment(sketch, "E7.5.4.3", {"start": v(819.15, 806.45) * mm, "end": v(838.2, 806.45) * mm});
            skLineSegment(sketch, "E7.5.5.0", {"start": v(838.2, 933.45) * mm, "end": v(838.2, 914.4) * mm});
            skLineSegment(sketch, "E7.5.5.1", {"start": v(819.15, 933.45) * mm, "end": v(819.15, 914.4) * mm});
            skLineSegment(sketch, "E7.5.5.2", {"start": v(819.15, 914.4) * mm, "end": v(838.2, 914.4) * mm});
            skLineSegment(sketch, "E7.5.5.3", {"start": v(819.15, 933.45) * mm, "end": v(838.2, 933.45) * mm});
            skLineSegment(sketch, "E7.5.6.0", {"start": v(838.2, 1060.45) * mm, "end": v(838.2, 1041.4) * mm});
            skLineSegment(sketch, "E7.5.6.1", {"start": v(819.15, 1060.45) * mm, "end": v(819.15, 1041.4) * mm});
            skLineSegment(sketch, "E7.5.6.2", {"start": v(819.15, 1041.4) * mm, "end": v(838.2, 1041.4) * mm});
            skLineSegment(sketch, "E7.5.6.3", {"start": v(819.15, 1060.45) * mm, "end": v(838.2, 1060.45) * mm});
            skLineSegment(sketch, "E7.5.7.0", {"start": v(838.2, 1187.45) * mm, "end": v(838.2, 1168.4) * mm});
            skLineSegment(sketch, "E7.5.7.1", {"start": v(819.15, 1187.45) * mm, "end": v(819.15, 1168.4) * mm});
            skLineSegment(sketch, "E7.5.7.2", {"start": v(819.15, 1168.4) * mm, "end": v(838.2, 1168.4) * mm});
            skLineSegment(sketch, "E7.5.7.3", {"start": v(819.15, 1187.45) * mm, "end": v(838.2, 1187.45) * mm});
            skLineSegment(sketch, "E7.5.8.0", {"start": v(838.2, 1314.45) * mm, "end": v(838.2, 1295.4) * mm});
            skLineSegment(sketch, "E7.5.8.1", {"start": v(819.15, 1314.45) * mm, "end": v(819.15, 1295.4) * mm});
            skLineSegment(sketch, "E7.5.8.2", {"start": v(819.15, 1295.4) * mm, "end": v(838.2, 1295.4) * mm});
            skLineSegment(sketch, "E7.5.8.3", {"start": v(819.15, 1314.45) * mm, "end": v(838.2, 1314.45) * mm});
            skLineSegment(sketch, "E7.6.0.0", {"start": v(984.25, 298.45) * mm, "end": v(984.25, 279.4) * mm});
            skLineSegment(sketch, "E7.6.0.1", {"start": v(965.2, 298.45) * mm, "end": v(965.2, 279.4) * mm});
            skLineSegment(sketch, "E7.6.0.2", {"start": v(965.2, 279.4) * mm, "end": v(984.25, 279.4) * mm});
            skLineSegment(sketch, "E7.6.0.3", {"start": v(965.2, 298.45) * mm, "end": v(984.25, 298.45) * mm});
            skLineSegment(sketch, "E7.6.1.0", {"start": v(984.25, 425.45) * mm, "end": v(984.25, 406.4) * mm});
            skLineSegment(sketch, "E7.6.1.1", {"start": v(965.2, 425.45) * mm, "end": v(965.2, 406.4) * mm});
            skLineSegment(sketch, "E7.6.1.2", {"start": v(965.2, 406.4) * mm, "end": v(984.25, 406.4) * mm});
            skLineSegment(sketch, "E7.6.1.3", {"start": v(965.2, 425.45) * mm, "end": v(984.25, 425.45) * mm});
            skLineSegment(sketch, "E7.6.2.0", {"start": v(984.25, 552.45) * mm, "end": v(984.25, 533.4) * mm});
            skLineSegment(sketch, "E7.6.2.1", {"start": v(965.2, 552.45) * mm, "end": v(965.2, 533.4) * mm});
            skLineSegment(sketch, "E7.6.2.2", {"start": v(965.2, 533.4) * mm, "end": v(984.25, 533.4) * mm});
            skLineSegment(sketch, "E7.6.2.3", {"start": v(965.2, 552.45) * mm, "end": v(984.25, 552.45) * mm});
            skLineSegment(sketch, "E7.6.3.0", {"start": v(984.25, 679.45) * mm, "end": v(984.25, 660.4) * mm});
            skLineSegment(sketch, "E7.6.3.1", {"start": v(965.2, 679.45) * mm, "end": v(965.2, 660.4) * mm});
            skLineSegment(sketch, "E7.6.3.2", {"start": v(965.2, 660.4) * mm, "end": v(984.25, 660.4) * mm});
            skLineSegment(sketch, "E7.6.3.3", {"start": v(965.2, 679.45) * mm, "end": v(984.25, 679.45) * mm});
            skLineSegment(sketch, "E7.6.4.0", {"start": v(984.25, 806.45) * mm, "end": v(984.25, 787.4) * mm});
            skLineSegment(sketch, "E7.6.4.1", {"start": v(965.2, 806.45) * mm, "end": v(965.2, 787.4) * mm});
            skLineSegment(sketch, "E7.6.4.2", {"start": v(965.2, 787.4) * mm, "end": v(984.25, 787.4) * mm});
            skLineSegment(sketch, "E7.6.4.3", {"start": v(965.2, 806.45) * mm, "end": v(984.25, 806.45) * mm});
            skLineSegment(sketch, "E7.6.5.0", {"start": v(984.25, 933.45) * mm, "end": v(984.25, 914.4) * mm});
            skLineSegment(sketch, "E7.6.5.1", {"start": v(965.2, 933.45) * mm, "end": v(965.2, 914.4) * mm});
            skLineSegment(sketch, "E7.6.5.2", {"start": v(965.2, 914.4) * mm, "end": v(984.25, 914.4) * mm});
            skLineSegment(sketch, "E7.6.5.3", {"start": v(965.2, 933.45) * mm, "end": v(984.25, 933.45) * mm});
            skLineSegment(sketch, "E7.6.6.0", {"start": v(984.25, 1060.45) * mm, "end": v(984.25, 1041.4) * mm});
            skLineSegment(sketch, "E7.6.6.1", {"start": v(965.2, 1060.45) * mm, "end": v(965.2, 1041.4) * mm});
            skLineSegment(sketch, "E7.6.6.2", {"start": v(965.2, 1041.4) * mm, "end": v(984.25, 1041.4) * mm});
            skLineSegment(sketch, "E7.6.6.3", {"start": v(965.2, 1060.45) * mm, "end": v(984.25, 1060.45) * mm});
            skLineSegment(sketch, "E7.6.7.0", {"start": v(984.25, 1187.45) * mm, "end": v(984.25, 1168.4) * mm});
            skLineSegment(sketch, "E7.6.7.1", {"start": v(965.2, 1187.45) * mm, "end": v(965.2, 1168.4) * mm});
            skLineSegment(sketch, "E7.6.7.2", {"start": v(965.2, 1168.4) * mm, "end": v(984.25, 1168.4) * mm});
            skLineSegment(sketch, "E7.6.7.3", {"start": v(965.2, 1187.45) * mm, "end": v(984.25, 1187.45) * mm});
            skLineSegment(sketch, "E7.6.8.0", {"start": v(984.25, 1314.45) * mm, "end": v(984.25, 1295.4) * mm});
            skLineSegment(sketch, "E7.6.8.1", {"start": v(965.2, 1314.45) * mm, "end": v(965.2, 1295.4) * mm});
            skLineSegment(sketch, "E7.6.8.2", {"start": v(965.2, 1295.4) * mm, "end": v(984.25, 1295.4) * mm});
            skLineSegment(sketch, "E7.6.8.3", {"start": v(965.2, 1314.45) * mm, "end": v(984.25, 1314.45) * mm});
            skLineSegment(sketch, "E7.7.0.0", {"start": v(1130.3, 298.45) * mm, "end": v(1130.3, 279.4) * mm});
            skLineSegment(sketch, "E7.7.0.1", {"start": v(1111.25, 298.45) * mm, "end": v(1111.25, 279.4) * mm});
            skLineSegment(sketch, "E7.7.0.2", {"start": v(1111.25, 279.4) * mm, "end": v(1130.3, 279.4) * mm});
            skLineSegment(sketch, "E7.7.0.3", {"start": v(1111.25, 298.45) * mm, "end": v(1130.3, 298.45) * mm});
            skLineSegment(sketch, "E7.7.1.0", {"start": v(1130.3, 425.45) * mm, "end": v(1130.3, 406.4) * mm});
            skLineSegment(sketch, "E7.7.1.1", {"start": v(1111.25, 425.45) * mm, "end": v(1111.25, 406.4) * mm});
            skLineSegment(sketch, "E7.7.1.2", {"start": v(1111.25, 406.4) * mm, "end": v(1130.3, 406.4) * mm});
            skLineSegment(sketch, "E7.7.1.3", {"start": v(1111.25, 425.45) * mm, "end": v(1130.3, 425.45) * mm});
            skLineSegment(sketch, "E7.7.2.0", {"start": v(1130.3, 552.45) * mm, "end": v(1130.3, 533.4) * mm});
            skLineSegment(sketch, "E7.7.2.1", {"start": v(1111.25, 552.45) * mm, "end": v(1111.25, 533.4) * mm});
            skLineSegment(sketch, "E7.7.2.2", {"start": v(1111.25, 533.4) * mm, "end": v(1130.3, 533.4) * mm});
            skLineSegment(sketch, "E7.7.2.3", {"start": v(1111.25, 552.45) * mm, "end": v(1130.3, 552.45) * mm});
            skLineSegment(sketch, "E7.7.3.0", {"start": v(1130.3, 679.45) * mm, "end": v(1130.3, 660.4) * mm});
            skLineSegment(sketch, "E7.7.3.1", {"start": v(1111.25, 679.45) * mm, "end": v(1111.25, 660.4) * mm});
            skLineSegment(sketch, "E7.7.3.2", {"start": v(1111.25, 660.4) * mm, "end": v(1130.3, 660.4) * mm});
            skLineSegment(sketch, "E7.7.3.3", {"start": v(1111.25, 679.45) * mm, "end": v(1130.3, 679.45) * mm});
            skLineSegment(sketch, "E7.7.4.0", {"start": v(1130.3, 806.45) * mm, "end": v(1130.3, 787.4) * mm});
            skLineSegment(sketch, "E7.7.4.1", {"start": v(1111.25, 806.45) * mm, "end": v(1111.25, 787.4) * mm});
            skLineSegment(sketch, "E7.7.4.2", {"start": v(1111.25, 787.4) * mm, "end": v(1130.3, 787.4) * mm});
            skLineSegment(sketch, "E7.7.4.3", {"start": v(1111.25, 806.45) * mm, "end": v(1130.3, 806.45) * mm});
            skLineSegment(sketch, "E7.7.5.0", {"start": v(1130.3, 933.45) * mm, "end": v(1130.3, 914.4) * mm});
            skLineSegment(sketch, "E7.7.5.1", {"start": v(1111.25, 933.45) * mm, "end": v(1111.25, 914.4) * mm});
            skLineSegment(sketch, "E7.7.5.2", {"start": v(1111.25, 914.4) * mm, "end": v(1130.3, 914.4) * mm});
            skLineSegment(sketch, "E7.7.5.3", {"start": v(1111.25, 933.45) * mm, "end": v(1130.3, 933.45) * mm});
            skLineSegment(sketch, "E7.7.6.0", {"start": v(1130.3, 1060.45) * mm, "end": v(1130.3, 1041.4) * mm});
            skLineSegment(sketch, "E7.7.6.1", {"start": v(1111.25, 1060.45) * mm, "end": v(1111.25, 1041.4) * mm});
            skLineSegment(sketch, "E7.7.6.2", {"start": v(1111.25, 1041.4) * mm, "end": v(1130.3, 1041.4) * mm});
            skLineSegment(sketch, "E7.7.6.3", {"start": v(1111.25, 1060.45) * mm, "end": v(1130.3, 1060.45) * mm});
            skLineSegment(sketch, "E7.7.7.0", {"start": v(1130.3, 1187.45) * mm, "end": v(1130.3, 1168.4) * mm});
            skLineSegment(sketch, "E7.7.7.1", {"start": v(1111.25, 1187.45) * mm, "end": v(1111.25, 1168.4) * mm});
            skLineSegment(sketch, "E7.7.7.2", {"start": v(1111.25, 1168.4) * mm, "end": v(1130.3, 1168.4) * mm});
            skLineSegment(sketch, "E7.7.7.3", {"start": v(1111.25, 1187.45) * mm, "end": v(1130.3, 1187.45) * mm});
            skLineSegment(sketch, "E7.7.8.0", {"start": v(1130.3, 1314.45) * mm, "end": v(1130.3, 1295.4) * mm});
            skLineSegment(sketch, "E7.7.8.1", {"start": v(1111.25, 1314.45) * mm, "end": v(1111.25, 1295.4) * mm});
            skLineSegment(sketch, "E7.7.8.2", {"start": v(1111.25, 1295.4) * mm, "end": v(1130.3, 1295.4) * mm});
            skLineSegment(sketch, "E7.7.8.3", {"start": v(1111.25, 1314.45) * mm, "end": v(1130.3, 1314.45) * mm});
            skLineSegment(sketch, "E7.8.0.0", {"start": v(1276.35, 298.45) * mm, "end": v(1276.35, 279.4) * mm});
            skLineSegment(sketch, "E7.8.0.1", {"start": v(1257.3, 298.45) * mm, "end": v(1257.3, 279.4) * mm});
            skLineSegment(sketch, "E7.8.0.2", {"start": v(1257.3, 279.4) * mm, "end": v(1276.35, 279.4) * mm});
            skLineSegment(sketch, "E7.8.0.3", {"start": v(1257.3, 298.45) * mm, "end": v(1276.35, 298.45) * mm});
            skLineSegment(sketch, "E7.8.1.0", {"start": v(1276.35, 425.45) * mm, "end": v(1276.35, 406.4) * mm});
            skLineSegment(sketch, "E7.8.1.1", {"start": v(1257.3, 425.45) * mm, "end": v(1257.3, 406.4) * mm});
            skLineSegment(sketch, "E7.8.1.2", {"start": v(1257.3, 406.4) * mm, "end": v(1276.35, 406.4) * mm});
            skLineSegment(sketch, "E7.8.1.3", {"start": v(1257.3, 425.45) * mm, "end": v(1276.35, 425.45) * mm});
            skLineSegment(sketch, "E7.8.2.0", {"start": v(1276.35, 552.45) * mm, "end": v(1276.35, 533.4) * mm});
            skLineSegment(sketch, "E7.8.2.1", {"start": v(1257.3, 552.45) * mm, "end": v(1257.3, 533.4) * mm});
            skLineSegment(sketch, "E7.8.2.2", {"start": v(1257.3, 533.4) * mm, "end": v(1276.35, 533.4) * mm});
            skLineSegment(sketch, "E7.8.2.3", {"start": v(1257.3, 552.45) * mm, "end": v(1276.35, 552.45) * mm});
            skLineSegment(sketch, "E7.8.3.0", {"start": v(1276.35, 679.45) * mm, "end": v(1276.35, 660.4) * mm});
            skLineSegment(sketch, "E7.8.3.1", {"start": v(1257.3, 679.45) * mm, "end": v(1257.3, 660.4) * mm});
            skLineSegment(sketch, "E7.8.3.2", {"start": v(1257.3, 660.4) * mm, "end": v(1276.35, 660.4) * mm});
            skLineSegment(sketch, "E7.8.3.3", {"start": v(1257.3, 679.45) * mm, "end": v(1276.35, 679.45) * mm});
            skLineSegment(sketch, "E7.8.4.0", {"start": v(1276.35, 806.45) * mm, "end": v(1276.35, 787.4) * mm});
            skLineSegment(sketch, "E7.8.4.1", {"start": v(1257.3, 806.45) * mm, "end": v(1257.3, 787.4) * mm});
            skLineSegment(sketch, "E7.8.4.2", {"start": v(1257.3, 787.4) * mm, "end": v(1276.35, 787.4) * mm});
            skLineSegment(sketch, "E7.8.4.3", {"start": v(1257.3, 806.45) * mm, "end": v(1276.35, 806.45) * mm});
            skLineSegment(sketch, "E7.8.5.0", {"start": v(1276.35, 933.45) * mm, "end": v(1276.35, 914.4) * mm});
            skLineSegment(sketch, "E7.8.5.1", {"start": v(1257.3, 933.45) * mm, "end": v(1257.3, 914.4) * mm});
            skLineSegment(sketch, "E7.8.5.2", {"start": v(1257.3, 914.4) * mm, "end": v(1276.35, 914.4) * mm});
            skLineSegment(sketch, "E7.8.5.3", {"start": v(1257.3, 933.45) * mm, "end": v(1276.35, 933.45) * mm});
            skLineSegment(sketch, "E7.8.6.0", {"start": v(1276.35, 1060.45) * mm, "end": v(1276.35, 1041.4) * mm});
            skLineSegment(sketch, "E7.8.6.1", {"start": v(1257.3, 1060.45) * mm, "end": v(1257.3, 1041.4) * mm});
            skLineSegment(sketch, "E7.8.6.2", {"start": v(1257.3, 1041.4) * mm, "end": v(1276.35, 1041.4) * mm});
            skLineSegment(sketch, "E7.8.6.3", {"start": v(1257.3, 1060.45) * mm, "end": v(1276.35, 1060.45) * mm});
            skLineSegment(sketch, "E7.8.7.0", {"start": v(1276.35, 1187.45) * mm, "end": v(1276.35, 1168.4) * mm});
            skLineSegment(sketch, "E7.8.7.1", {"start": v(1257.3, 1187.45) * mm, "end": v(1257.3, 1168.4) * mm});
            skLineSegment(sketch, "E7.8.7.2", {"start": v(1257.3, 1168.4) * mm, "end": v(1276.35, 1168.4) * mm});
            skLineSegment(sketch, "E7.8.7.3", {"start": v(1257.3, 1187.45) * mm, "end": v(1276.35, 1187.45) * mm});
            skLineSegment(sketch, "E7.8.8.0", {"start": v(1276.35, 1314.45) * mm, "end": v(1276.35, 1295.4) * mm});
            skLineSegment(sketch, "E7.8.8.1", {"start": v(1257.3, 1314.45) * mm, "end": v(1257.3, 1295.4) * mm});
            skLineSegment(sketch, "E7.8.8.2", {"start": v(1257.3, 1295.4) * mm, "end": v(1276.35, 1295.4) * mm});
            skLineSegment(sketch, "E7.8.8.3", {"start": v(1257.3, 1314.45) * mm, "end": v(1276.35, 1314.45) * mm});
            skLineSegment(sketch, "E7.9.0.0", {"start": v(1422.4, 298.45) * mm, "end": v(1422.4, 279.4) * mm});
            skLineSegment(sketch, "E7.9.0.1", {"start": v(1403.35, 298.45) * mm, "end": v(1403.35, 279.4) * mm});
            skLineSegment(sketch, "E7.9.0.2", {"start": v(1403.35, 279.4) * mm, "end": v(1422.4, 279.4) * mm});
            skLineSegment(sketch, "E7.9.0.3", {"start": v(1403.35, 298.45) * mm, "end": v(1422.4, 298.45) * mm});
            skLineSegment(sketch, "E7.9.1.0", {"start": v(1422.4, 425.45) * mm, "end": v(1422.4, 406.4) * mm});
            skLineSegment(sketch, "E7.9.1.1", {"start": v(1403.35, 425.45) * mm, "end": v(1403.35, 406.4) * mm});
            skLineSegment(sketch, "E7.9.1.2", {"start": v(1403.35, 406.4) * mm, "end": v(1422.4, 406.4) * mm});
            skLineSegment(sketch, "E7.9.1.3", {"start": v(1403.35, 425.45) * mm, "end": v(1422.4, 425.45) * mm});
            skLineSegment(sketch, "E7.9.2.0", {"start": v(1422.4, 552.45) * mm, "end": v(1422.4, 533.4) * mm});
            skLineSegment(sketch, "E7.9.2.1", {"start": v(1403.35, 552.45) * mm, "end": v(1403.35, 533.4) * mm});
            skLineSegment(sketch, "E7.9.2.2", {"start": v(1403.35, 533.4) * mm, "end": v(1422.4, 533.4) * mm});
            skLineSegment(sketch, "E7.9.2.3", {"start": v(1403.35, 552.45) * mm, "end": v(1422.4, 552.45) * mm});
            skLineSegment(sketch, "E7.9.3.0", {"start": v(1422.4, 679.45) * mm, "end": v(1422.4, 660.4) * mm});
            skLineSegment(sketch, "E7.9.3.1", {"start": v(1403.35, 679.45) * mm, "end": v(1403.35, 660.4) * mm});
            skLineSegment(sketch, "E7.9.3.2", {"start": v(1403.35, 660.4) * mm, "end": v(1422.4, 660.4) * mm});
            skLineSegment(sketch, "E7.9.3.3", {"start": v(1403.35, 679.45) * mm, "end": v(1422.4, 679.45) * mm});
            skLineSegment(sketch, "E7.9.4.0", {"start": v(1422.4, 806.45) * mm, "end": v(1422.4, 787.4) * mm});
            skLineSegment(sketch, "E7.9.4.1", {"start": v(1403.35, 806.45) * mm, "end": v(1403.35, 787.4) * mm});
            skLineSegment(sketch, "E7.9.4.2", {"start": v(1403.35, 787.4) * mm, "end": v(1422.4, 787.4) * mm});
            skLineSegment(sketch, "E7.9.4.3", {"start": v(1403.35, 806.45) * mm, "end": v(1422.4, 806.45) * mm});
            skLineSegment(sketch, "E7.9.5.0", {"start": v(1422.4, 933.45) * mm, "end": v(1422.4, 914.4) * mm});
            skLineSegment(sketch, "E7.9.5.1", {"start": v(1403.35, 933.45) * mm, "end": v(1403.35, 914.4) * mm});
            skLineSegment(sketch, "E7.9.5.2", {"start": v(1403.35, 914.4) * mm, "end": v(1422.4, 914.4) * mm});
            skLineSegment(sketch, "E7.9.5.3", {"start": v(1403.35, 933.45) * mm, "end": v(1422.4, 933.45) * mm});
            skLineSegment(sketch, "E7.9.6.0", {"start": v(1422.4, 1060.45) * mm, "end": v(1422.4, 1041.4) * mm});
            skLineSegment(sketch, "E7.9.6.1", {"start": v(1403.35, 1060.45) * mm, "end": v(1403.35, 1041.4) * mm});
            skLineSegment(sketch, "E7.9.6.2", {"start": v(1403.35, 1041.4) * mm, "end": v(1422.4, 1041.4) * mm});
            skLineSegment(sketch, "E7.9.6.3", {"start": v(1403.35, 1060.45) * mm, "end": v(1422.4, 1060.45) * mm});
            skLineSegment(sketch, "E7.9.7.0", {"start": v(1422.4, 1187.45) * mm, "end": v(1422.4, 1168.4) * mm});
            skLineSegment(sketch, "E7.9.7.1", {"start": v(1403.35, 1187.45) * mm, "end": v(1403.35, 1168.4) * mm});
            skLineSegment(sketch, "E7.9.7.2", {"start": v(1403.35, 1168.4) * mm, "end": v(1422.4, 1168.4) * mm});
            skLineSegment(sketch, "E7.9.7.3", {"start": v(1403.35, 1187.45) * mm, "end": v(1422.4, 1187.45) * mm});
            skLineSegment(sketch, "E7.9.8.0", {"start": v(1422.4, 1314.45) * mm, "end": v(1422.4, 1295.4) * mm});
            skLineSegment(sketch, "E7.9.8.1", {"start": v(1403.35, 1314.45) * mm, "end": v(1403.35, 1295.4) * mm});
            skLineSegment(sketch, "E7.9.8.2", {"start": v(1403.35, 1295.4) * mm, "end": v(1422.4, 1295.4) * mm});
            skLineSegment(sketch, "E7.9.8.3", {"start": v(1403.35, 1314.45) * mm, "end": v(1422.4, 1314.45) * mm});
            skLineSegment(sketch, "E7.10.0.0", {"start": v(1568.45, 298.45) * mm, "end": v(1568.45, 279.4) * mm});
            skLineSegment(sketch, "E7.10.0.1", {"start": v(1549.4, 298.45) * mm, "end": v(1549.4, 279.4) * mm});
            skLineSegment(sketch, "E7.10.0.2", {"start": v(1549.4, 279.4) * mm, "end": v(1568.45, 279.4) * mm});
            skLineSegment(sketch, "E7.10.0.3", {"start": v(1549.4, 298.45) * mm, "end": v(1568.45, 298.45) * mm});
            skLineSegment(sketch, "E7.10.1.0", {"start": v(1568.45, 425.45) * mm, "end": v(1568.45, 406.4) * mm});
            skLineSegment(sketch, "E7.10.1.1", {"start": v(1549.4, 425.45) * mm, "end": v(1549.4, 406.4) * mm});
            skLineSegment(sketch, "E7.10.1.2", {"start": v(1549.4, 406.4) * mm, "end": v(1568.45, 406.4) * mm});
            skLineSegment(sketch, "E7.10.1.3", {"start": v(1549.4, 425.45) * mm, "end": v(1568.45, 425.45) * mm});
            skLineSegment(sketch, "E7.10.2.0", {"start": v(1568.45, 552.45) * mm, "end": v(1568.45, 533.4) * mm});
            skLineSegment(sketch, "E7.10.2.1", {"start": v(1549.4, 552.45) * mm, "end": v(1549.4, 533.4) * mm});
            skLineSegment(sketch, "E7.10.2.2", {"start": v(1549.4, 533.4) * mm, "end": v(1568.45, 533.4) * mm});
            skLineSegment(sketch, "E7.10.2.3", {"start": v(1549.4, 552.45) * mm, "end": v(1568.45, 552.45) * mm});
            skLineSegment(sketch, "E7.10.3.0", {"start": v(1568.45, 679.45) * mm, "end": v(1568.45, 660.4) * mm});
            skLineSegment(sketch, "E7.10.3.1", {"start": v(1549.4, 679.45) * mm, "end": v(1549.4, 660.4) * mm});
            skLineSegment(sketch, "E7.10.3.2", {"start": v(1549.4, 660.4) * mm, "end": v(1568.45, 660.4) * mm});
            skLineSegment(sketch, "E7.10.3.3", {"start": v(1549.4, 679.45) * mm, "end": v(1568.45, 679.45) * mm});
            skLineSegment(sketch, "E7.10.4.0", {"start": v(1568.45, 806.45) * mm, "end": v(1568.45, 787.4) * mm});
            skLineSegment(sketch, "E7.10.4.1", {"start": v(1549.4, 806.45) * mm, "end": v(1549.4, 787.4) * mm});
            skLineSegment(sketch, "E7.10.4.2", {"start": v(1549.4, 787.4) * mm, "end": v(1568.45, 787.4) * mm});
            skLineSegment(sketch, "E7.10.4.3", {"start": v(1549.4, 806.45) * mm, "end": v(1568.45, 806.45) * mm});
            skLineSegment(sketch, "E7.10.5.0", {"start": v(1568.45, 933.45) * mm, "end": v(1568.45, 914.4) * mm});
            skLineSegment(sketch, "E7.10.5.1", {"start": v(1549.4, 933.45) * mm, "end": v(1549.4, 914.4) * mm});
            skLineSegment(sketch, "E7.10.5.2", {"start": v(1549.4, 914.4) * mm, "end": v(1568.45, 914.4) * mm});
            skLineSegment(sketch, "E7.10.5.3", {"start": v(1549.4, 933.45) * mm, "end": v(1568.45, 933.45) * mm});
            skLineSegment(sketch, "E7.10.6.0", {"start": v(1568.45, 1060.45) * mm, "end": v(1568.45, 1041.4) * mm});
            skLineSegment(sketch, "E7.10.6.1", {"start": v(1549.4, 1060.45) * mm, "end": v(1549.4, 1041.4) * mm});
            skLineSegment(sketch, "E7.10.6.2", {"start": v(1549.4, 1041.4) * mm, "end": v(1568.45, 1041.4) * mm});
            skLineSegment(sketch, "E7.10.6.3", {"start": v(1549.4, 1060.45) * mm, "end": v(1568.45, 1060.45) * mm});
            skLineSegment(sketch, "E7.10.7.0", {"start": v(1568.45, 1187.45) * mm, "end": v(1568.45, 1168.4) * mm});
            skLineSegment(sketch, "E7.10.7.1", {"start": v(1549.4, 1187.45) * mm, "end": v(1549.4, 1168.4) * mm});
            skLineSegment(sketch, "E7.10.7.2", {"start": v(1549.4, 1168.4) * mm, "end": v(1568.45, 1168.4) * mm});
            skLineSegment(sketch, "E7.10.7.3", {"start": v(1549.4, 1187.45) * mm, "end": v(1568.45, 1187.45) * mm});
            skLineSegment(sketch, "E7.10.8.0", {"start": v(1568.45, 1314.45) * mm, "end": v(1568.45, 1295.4) * mm});
            skLineSegment(sketch, "E7.10.8.1", {"start": v(1549.4, 1314.45) * mm, "end": v(1549.4, 1295.4) * mm});
            skLineSegment(sketch, "E7.10.8.2", {"start": v(1549.4, 1295.4) * mm, "end": v(1568.45, 1295.4) * mm});
            skLineSegment(sketch, "E7.10.8.3", {"start": v(1549.4, 1314.45) * mm, "end": v(1568.45, 1314.45) * mm});
            skLineSegment(sketch, "E7.direction1", {"start": v(88.9, 279.4) * mm, "end": v(234.95, 279.4) * mm, "construction": true});
            skLineSegment(sketch, "E7.direction2", {"start": v(88.9, 279.4) * mm, "end": v(88.9, 406.4) * mm, "construction": true});
            skLineSegment(sketch, "E8.0.0.9", {"start": v(107.95, 1441.45) * mm, "end": v(107.95, 1422.4) * mm});
            skLineSegment(sketch, "E8.3.0.9", {"start": v(88.9, 1441.45) * mm, "end": v(88.9, 1422.4) * mm});
            skLineSegment(sketch, "E8.6.0.9", {"start": v(88.9, 1422.4) * mm, "end": v(107.95, 1422.4) * mm});
            skLineSegment(sketch, "E8.9.0.9", {"start": v(88.9, 1441.45) * mm, "end": v(107.95, 1441.45) * mm});
            skLineSegment(sketch, "E8.0.1.9", {"start": v(254, 1441.45) * mm, "end": v(254, 1422.4) * mm});
            skLineSegment(sketch, "E8.3.1.9", {"start": v(234.95, 1441.45) * mm, "end": v(234.95, 1422.4) * mm});
            skLineSegment(sketch, "E8.6.1.9", {"start": v(234.95, 1422.4) * mm, "end": v(254, 1422.4) * mm});
            skLineSegment(sketch, "E8.9.1.9", {"start": v(234.95, 1441.45) * mm, "end": v(254, 1441.45) * mm});
            skLineSegment(sketch, "E8.0.2.9", {"start": v(400.05, 1441.45) * mm, "end": v(400.05, 1422.4) * mm});
            skLineSegment(sketch, "E8.3.2.9", {"start": v(381, 1441.45) * mm, "end": v(381, 1422.4) * mm});
            skLineSegment(sketch, "E8.6.2.9", {"start": v(381, 1422.4) * mm, "end": v(400.05, 1422.4) * mm});
            skLineSegment(sketch, "E8.9.2.9", {"start": v(381, 1441.45) * mm, "end": v(400.05, 1441.45) * mm});
            skLineSegment(sketch, "E8.0.3.9", {"start": v(546.1, 1441.45) * mm, "end": v(546.1, 1422.4) * mm});
            skLineSegment(sketch, "E8.3.3.9", {"start": v(527.05, 1441.45) * mm, "end": v(527.05, 1422.4) * mm});
            skLineSegment(sketch, "E8.6.3.9", {"start": v(527.05, 1422.4) * mm, "end": v(546.1, 1422.4) * mm});
            skLineSegment(sketch, "E8.9.3.9", {"start": v(527.05, 1441.45) * mm, "end": v(546.1, 1441.45) * mm});
            skLineSegment(sketch, "E8.0.4.9", {"start": v(692.15, 1441.45) * mm, "end": v(692.15, 1422.4) * mm});
            skLineSegment(sketch, "E8.3.4.9", {"start": v(673.1, 1441.45) * mm, "end": v(673.1, 1422.4) * mm});
            skLineSegment(sketch, "E8.6.4.9", {"start": v(673.1, 1422.4) * mm, "end": v(692.15, 1422.4) * mm});
            skLineSegment(sketch, "E8.9.4.9", {"start": v(673.1, 1441.45) * mm, "end": v(692.15, 1441.45) * mm});
            skLineSegment(sketch, "E8.0.5.9", {"start": v(838.2, 1441.45) * mm, "end": v(838.2, 1422.4) * mm});
            skLineSegment(sketch, "E8.3.5.9", {"start": v(819.15, 1441.45) * mm, "end": v(819.15, 1422.4) * mm});
            skLineSegment(sketch, "E8.6.5.9", {"start": v(819.15, 1422.4) * mm, "end": v(838.2, 1422.4) * mm});
            skLineSegment(sketch, "E8.9.5.9", {"start": v(819.15, 1441.45) * mm, "end": v(838.2, 1441.45) * mm});
            skLineSegment(sketch, "E8.0.6.9", {"start": v(984.25, 1441.45) * mm, "end": v(984.25, 1422.4) * mm});
            skLineSegment(sketch, "E8.3.6.9", {"start": v(965.2, 1441.45) * mm, "end": v(965.2, 1422.4) * mm});
            skLineSegment(sketch, "E8.6.6.9", {"start": v(965.2, 1422.4) * mm, "end": v(984.25, 1422.4) * mm});
            skLineSegment(sketch, "E8.9.6.9", {"start": v(965.2, 1441.45) * mm, "end": v(984.25, 1441.45) * mm});
            skLineSegment(sketch, "E8.0.7.9", {"start": v(1130.3, 1441.45) * mm, "end": v(1130.3, 1422.4) * mm});
            skLineSegment(sketch, "E8.3.7.9", {"start": v(1111.25, 1441.45) * mm, "end": v(1111.25, 1422.4) * mm});
            skLineSegment(sketch, "E8.6.7.9", {"start": v(1111.25, 1422.4) * mm, "end": v(1130.3, 1422.4) * mm});
            skLineSegment(sketch, "E8.9.7.9", {"start": v(1111.25, 1441.45) * mm, "end": v(1130.3, 1441.45) * mm});
            skLineSegment(sketch, "E8.0.8.9", {"start": v(1276.35, 1441.45) * mm, "end": v(1276.35, 1422.4) * mm});
            skLineSegment(sketch, "E8.3.8.9", {"start": v(1257.3, 1441.45) * mm, "end": v(1257.3, 1422.4) * mm});
            skLineSegment(sketch, "E8.6.8.9", {"start": v(1257.3, 1422.4) * mm, "end": v(1276.35, 1422.4) * mm});
            skLineSegment(sketch, "E8.9.8.9", {"start": v(1257.3, 1441.45) * mm, "end": v(1276.35, 1441.45) * mm});
            skLineSegment(sketch, "E8.0.9.9", {"start": v(1422.4, 1441.45) * mm, "end": v(1422.4, 1422.4) * mm});
            skLineSegment(sketch, "E8.3.9.9", {"start": v(1403.35, 1441.45) * mm, "end": v(1403.35, 1422.4) * mm});
            skLineSegment(sketch, "E8.6.9.9", {"start": v(1403.35, 1422.4) * mm, "end": v(1422.4, 1422.4) * mm});
            skLineSegment(sketch, "E8.9.9.9", {"start": v(1403.35, 1441.45) * mm, "end": v(1422.4, 1441.45) * mm});
            skLineSegment(sketch, "E8.0.10.9", {"start": v(1568.45, 1441.45) * mm, "end": v(1568.45, 1422.4) * mm});
            skLineSegment(sketch, "E8.3.10.9", {"start": v(1549.4, 1441.45) * mm, "end": v(1549.4, 1422.4) * mm});
            skLineSegment(sketch, "E8.6.10.9", {"start": v(1549.4, 1422.4) * mm, "end": v(1568.45, 1422.4) * mm});
            skLineSegment(sketch, "E8.9.10.9", {"start": v(1549.4, 1441.45) * mm, "end": v(1568.45, 1441.45) * mm});
            skLineSegment(sketch, "E9.bottom", {"start": v(196.85, 298.45) * mm, "end": v(177.8, 298.45) * mm});
            skLineSegment(sketch, "E9.top", {"start": v(196.85, 279.4) * mm, "end": v(177.8, 279.4) * mm});
            skLineSegment(sketch, "E9.left", {"start": v(196.85, 298.45) * mm, "end": v(196.85, 279.4) * mm});
            skLineSegment(sketch, "E9.right", {"start": v(177.8, 298.45) * mm, "end": v(177.8, 279.4) * mm});
            skLineSegment(sketch, "E10.0.1.0", {"start": v(196.85, 425.45) * mm, "end": v(196.85, 406.4) * mm});
            skLineSegment(sketch, "E10.0.1.1", {"start": v(177.8, 425.45) * mm, "end": v(177.8, 406.4) * mm});
            skLineSegment(sketch, "E10.0.1.2", {"start": v(196.85, 406.4) * mm, "end": v(177.8, 406.4) * mm});
            skLineSegment(sketch, "E10.0.1.3", {"start": v(196.85, 425.45) * mm, "end": v(177.8, 425.45) * mm});
            skLineSegment(sketch, "E10.0.2.0", {"start": v(196.85, 552.45) * mm, "end": v(196.85, 533.4) * mm});
            skLineSegment(sketch, "E10.0.2.1", {"start": v(177.8, 552.45) * mm, "end": v(177.8, 533.4) * mm});
            skLineSegment(sketch, "E10.0.2.2", {"start": v(196.85, 533.4) * mm, "end": v(177.8, 533.4) * mm});
            skLineSegment(sketch, "E10.0.2.3", {"start": v(196.85, 552.45) * mm, "end": v(177.8, 552.45) * mm});
            skLineSegment(sketch, "E10.0.3.0", {"start": v(196.85, 679.45) * mm, "end": v(196.85, 660.4) * mm});
            skLineSegment(sketch, "E10.0.3.1", {"start": v(177.8, 679.45) * mm, "end": v(177.8, 660.4) * mm});
            skLineSegment(sketch, "E10.0.3.2", {"start": v(196.85, 660.4) * mm, "end": v(177.8, 660.4) * mm});
            skLineSegment(sketch, "E10.0.3.3", {"start": v(196.85, 679.45) * mm, "end": v(177.8, 679.45) * mm});
            skLineSegment(sketch, "E10.0.4.0", {"start": v(196.85, 806.45) * mm, "end": v(196.85, 787.4) * mm});
            skLineSegment(sketch, "E10.0.4.1", {"start": v(177.8, 806.45) * mm, "end": v(177.8, 787.4) * mm});
            skLineSegment(sketch, "E10.0.4.2", {"start": v(196.85, 787.4) * mm, "end": v(177.8, 787.4) * mm});
            skLineSegment(sketch, "E10.0.4.3", {"start": v(196.85, 806.45) * mm, "end": v(177.8, 806.45) * mm});
            skLineSegment(sketch, "E10.0.5.0", {"start": v(196.85, 933.45) * mm, "end": v(196.85, 914.4) * mm});
            skLineSegment(sketch, "E10.0.5.1", {"start": v(177.8, 933.45) * mm, "end": v(177.8, 914.4) * mm});
            skLineSegment(sketch, "E10.0.5.2", {"start": v(196.85, 914.4) * mm, "end": v(177.8, 914.4) * mm});
            skLineSegment(sketch, "E10.0.5.3", {"start": v(196.85, 933.45) * mm, "end": v(177.8, 933.45) * mm});
            skLineSegment(sketch, "E10.0.6.0", {"start": v(196.85, 1060.45) * mm, "end": v(196.85, 1041.4) * mm});
            skLineSegment(sketch, "E10.0.6.1", {"start": v(177.8, 1060.45) * mm, "end": v(177.8, 1041.4) * mm});
            skLineSegment(sketch, "E10.0.6.2", {"start": v(196.85, 1041.4) * mm, "end": v(177.8, 1041.4) * mm});
            skLineSegment(sketch, "E10.0.6.3", {"start": v(196.85, 1060.45) * mm, "end": v(177.8, 1060.45) * mm});
            skLineSegment(sketch, "E10.0.7.0", {"start": v(196.85, 1187.45) * mm, "end": v(196.85, 1168.4) * mm});
            skLineSegment(sketch, "E10.0.7.1", {"start": v(177.8, 1187.45) * mm, "end": v(177.8, 1168.4) * mm});
            skLineSegment(sketch, "E10.0.7.2", {"start": v(196.85, 1168.4) * mm, "end": v(177.8, 1168.4) * mm});
            skLineSegment(sketch, "E10.0.7.3", {"start": v(196.85, 1187.45) * mm, "end": v(177.8, 1187.45) * mm});
            skLineSegment(sketch, "E10.0.8.0", {"start": v(196.85, 1314.45) * mm, "end": v(196.85, 1295.4) * mm});
            skLineSegment(sketch, "E10.0.8.1", {"start": v(177.8, 1314.45) * mm, "end": v(177.8, 1295.4) * mm});
            skLineSegment(sketch, "E10.0.8.2", {"start": v(196.85, 1295.4) * mm, "end": v(177.8, 1295.4) * mm});
            skLineSegment(sketch, "E10.0.8.3", {"start": v(196.85, 1314.45) * mm, "end": v(177.8, 1314.45) * mm});
            skLineSegment(sketch, "E10.0.9.0", {"start": v(196.85, 1441.45) * mm, "end": v(196.85, 1422.4) * mm});
            skLineSegment(sketch, "E10.0.9.1", {"start": v(177.8, 1441.45) * mm, "end": v(177.8, 1422.4) * mm});
            skLineSegment(sketch, "E10.0.9.2", {"start": v(196.85, 1422.4) * mm, "end": v(177.8, 1422.4) * mm});
            skLineSegment(sketch, "E10.0.9.3", {"start": v(196.85, 1441.45) * mm, "end": v(177.8, 1441.45) * mm});
            skLineSegment(sketch, "E10.1.0.0", {"start": v(342.9, 298.45) * mm, "end": v(342.9, 279.4) * mm});
            skLineSegment(sketch, "E10.1.0.1", {"start": v(323.85, 298.45) * mm, "end": v(323.85, 279.4) * mm});
            skLineSegment(sketch, "E10.1.0.2", {"start": v(342.9, 279.4) * mm, "end": v(323.85, 279.4) * mm});
            skLineSegment(sketch, "E10.1.0.3", {"start": v(342.9, 298.45) * mm, "end": v(323.85, 298.45) * mm});
            skLineSegment(sketch, "E10.1.1.0", {"start": v(342.9, 425.45) * mm, "end": v(342.9, 406.4) * mm});
            skLineSegment(sketch, "E10.1.1.1", {"start": v(323.85, 425.45) * mm, "end": v(323.85, 406.4) * mm});
            skLineSegment(sketch, "E10.1.1.2", {"start": v(342.9, 406.4) * mm, "end": v(323.85, 406.4) * mm});
            skLineSegment(sketch, "E10.1.1.3", {"start": v(342.9, 425.45) * mm, "end": v(323.85, 425.45) * mm});
            skLineSegment(sketch, "E10.1.2.0", {"start": v(342.9, 552.45) * mm, "end": v(342.9, 533.4) * mm});
            skLineSegment(sketch, "E10.1.2.1", {"start": v(323.85, 552.45) * mm, "end": v(323.85, 533.4) * mm});
            skLineSegment(sketch, "E10.1.2.2", {"start": v(342.9, 533.4) * mm, "end": v(323.85, 533.4) * mm});
            skLineSegment(sketch, "E10.1.2.3", {"start": v(342.9, 552.45) * mm, "end": v(323.85, 552.45) * mm});
            skLineSegment(sketch, "E10.1.3.0", {"start": v(342.9, 679.45) * mm, "end": v(342.9, 660.4) * mm});
            skLineSegment(sketch, "E10.1.3.1", {"start": v(323.85, 679.45) * mm, "end": v(323.85, 660.4) * mm});
            skLineSegment(sketch, "E10.1.3.2", {"start": v(342.9, 660.4) * mm, "end": v(323.85, 660.4) * mm});
            skLineSegment(sketch, "E10.1.3.3", {"start": v(342.9, 679.45) * mm, "end": v(323.85, 679.45) * mm});
            skLineSegment(sketch, "E10.1.4.0", {"start": v(342.9, 806.45) * mm, "end": v(342.9, 787.4) * mm});
            skLineSegment(sketch, "E10.1.4.1", {"start": v(323.85, 806.45) * mm, "end": v(323.85, 787.4) * mm});
            skLineSegment(sketch, "E10.1.4.2", {"start": v(342.9, 787.4) * mm, "end": v(323.85, 787.4) * mm});
            skLineSegment(sketch, "E10.1.4.3", {"start": v(342.9, 806.45) * mm, "end": v(323.85, 806.45) * mm});
            skLineSegment(sketch, "E10.1.5.0", {"start": v(342.9, 933.45) * mm, "end": v(342.9, 914.4) * mm});
            skLineSegment(sketch, "E10.1.5.1", {"start": v(323.85, 933.45) * mm, "end": v(323.85, 914.4) * mm});
            skLineSegment(sketch, "E10.1.5.2", {"start": v(342.9, 914.4) * mm, "end": v(323.85, 914.4) * mm});
            skLineSegment(sketch, "E10.1.5.3", {"start": v(342.9, 933.45) * mm, "end": v(323.85, 933.45) * mm});
            skLineSegment(sketch, "E10.1.6.0", {"start": v(342.9, 1060.45) * mm, "end": v(342.9, 1041.4) * mm});
            skLineSegment(sketch, "E10.1.6.1", {"start": v(323.85, 1060.45) * mm, "end": v(323.85, 1041.4) * mm});
            skLineSegment(sketch, "E10.1.6.2", {"start": v(342.9, 1041.4) * mm, "end": v(323.85, 1041.4) * mm});
            skLineSegment(sketch, "E10.1.6.3", {"start": v(342.9, 1060.45) * mm, "end": v(323.85, 1060.45) * mm});
            skLineSegment(sketch, "E10.1.7.0", {"start": v(342.9, 1187.45) * mm, "end": v(342.9, 1168.4) * mm});
            skLineSegment(sketch, "E10.1.7.1", {"start": v(323.85, 1187.45) * mm, "end": v(323.85, 1168.4) * mm});
            skLineSegment(sketch, "E10.1.7.2", {"start": v(342.9, 1168.4) * mm, "end": v(323.85, 1168.4) * mm});
            skLineSegment(sketch, "E10.1.7.3", {"start": v(342.9, 1187.45) * mm, "end": v(323.85, 1187.45) * mm});
            skLineSegment(sketch, "E10.1.8.0", {"start": v(342.9, 1314.45) * mm, "end": v(342.9, 1295.4) * mm});
            skLineSegment(sketch, "E10.1.8.1", {"start": v(323.85, 1314.45) * mm, "end": v(323.85, 1295.4) * mm});
            skLineSegment(sketch, "E10.1.8.2", {"start": v(342.9, 1295.4) * mm, "end": v(323.85, 1295.4) * mm});
            skLineSegment(sketch, "E10.1.8.3", {"start": v(342.9, 1314.45) * mm, "end": v(323.85, 1314.45) * mm});
            skLineSegment(sketch, "E10.1.9.0", {"start": v(342.9, 1441.45) * mm, "end": v(342.9, 1422.4) * mm});
            skLineSegment(sketch, "E10.1.9.1", {"start": v(323.85, 1441.45) * mm, "end": v(323.85, 1422.4) * mm});
            skLineSegment(sketch, "E10.1.9.2", {"start": v(342.9, 1422.4) * mm, "end": v(323.85, 1422.4) * mm});
            skLineSegment(sketch, "E10.1.9.3", {"start": v(342.9, 1441.45) * mm, "end": v(323.85, 1441.45) * mm});
            skLineSegment(sketch, "E10.2.0.0", {"start": v(488.95, 298.45) * mm, "end": v(488.95, 279.4) * mm});
            skLineSegment(sketch, "E10.2.0.1", {"start": v(469.9, 298.45) * mm, "end": v(469.9, 279.4) * mm});
            skLineSegment(sketch, "E10.2.0.2", {"start": v(488.95, 279.4) * mm, "end": v(469.9, 279.4) * mm});
            skLineSegment(sketch, "E10.2.0.3", {"start": v(488.95, 298.45) * mm, "end": v(469.9, 298.45) * mm});
            skLineSegment(sketch, "E10.2.1.0", {"start": v(488.95, 425.45) * mm, "end": v(488.95, 406.4) * mm});
            skLineSegment(sketch, "E10.2.1.1", {"start": v(469.9, 425.45) * mm, "end": v(469.9, 406.4) * mm});
            skLineSegment(sketch, "E10.2.1.2", {"start": v(488.95, 406.4) * mm, "end": v(469.9, 406.4) * mm});
            skLineSegment(sketch, "E10.2.1.3", {"start": v(488.95, 425.45) * mm, "end": v(469.9, 425.45) * mm});
            skLineSegment(sketch, "E10.2.2.0", {"start": v(488.95, 552.45) * mm, "end": v(488.95, 533.4) * mm});
            skLineSegment(sketch, "E10.2.2.1", {"start": v(469.9, 552.45) * mm, "end": v(469.9, 533.4) * mm});
            skLineSegment(sketch, "E10.2.2.2", {"start": v(488.95, 533.4) * mm, "end": v(469.9, 533.4) * mm});
            skLineSegment(sketch, "E10.2.2.3", {"start": v(488.95, 552.45) * mm, "end": v(469.9, 552.45) * mm});
            skLineSegment(sketch, "E10.2.3.0", {"start": v(488.95, 679.45) * mm, "end": v(488.95, 660.4) * mm});
            skLineSegment(sketch, "E10.2.3.1", {"start": v(469.9, 679.45) * mm, "end": v(469.9, 660.4) * mm});
            skLineSegment(sketch, "E10.2.3.2", {"start": v(488.95, 660.4) * mm, "end": v(469.9, 660.4) * mm});
            skLineSegment(sketch, "E10.2.3.3", {"start": v(488.95, 679.45) * mm, "end": v(469.9, 679.45) * mm});
            skLineSegment(sketch, "E10.2.4.0", {"start": v(488.95, 806.45) * mm, "end": v(488.95, 787.4) * mm});
            skLineSegment(sketch, "E10.2.4.1", {"start": v(469.9, 806.45) * mm, "end": v(469.9, 787.4) * mm});
            skLineSegment(sketch, "E10.2.4.2", {"start": v(488.95, 787.4) * mm, "end": v(469.9, 787.4) * mm});
            skLineSegment(sketch, "E10.2.4.3", {"start": v(488.95, 806.45) * mm, "end": v(469.9, 806.45) * mm});
            skLineSegment(sketch, "E10.2.5.0", {"start": v(488.95, 933.45) * mm, "end": v(488.95, 914.4) * mm});
            skLineSegment(sketch, "E10.2.5.1", {"start": v(469.9, 933.45) * mm, "end": v(469.9, 914.4) * mm});
            skLineSegment(sketch, "E10.2.5.2", {"start": v(488.95, 914.4) * mm, "end": v(469.9, 914.4) * mm});
            skLineSegment(sketch, "E10.2.5.3", {"start": v(488.95, 933.45) * mm, "end": v(469.9, 933.45) * mm});
            skLineSegment(sketch, "E10.2.6.0", {"start": v(488.95, 1060.45) * mm, "end": v(488.95, 1041.4) * mm});
            skLineSegment(sketch, "E10.2.6.1", {"start": v(469.9, 1060.45) * mm, "end": v(469.9, 1041.4) * mm});
            skLineSegment(sketch, "E10.2.6.2", {"start": v(488.95, 1041.4) * mm, "end": v(469.9, 1041.4) * mm});
            skLineSegment(sketch, "E10.2.6.3", {"start": v(488.95, 1060.45) * mm, "end": v(469.9, 1060.45) * mm});
            skLineSegment(sketch, "E10.2.7.0", {"start": v(488.95, 1187.45) * mm, "end": v(488.95, 1168.4) * mm});
            skLineSegment(sketch, "E10.2.7.1", {"start": v(469.9, 1187.45) * mm, "end": v(469.9, 1168.4) * mm});
            skLineSegment(sketch, "E10.2.7.2", {"start": v(488.95, 1168.4) * mm, "end": v(469.9, 1168.4) * mm});
            skLineSegment(sketch, "E10.2.7.3", {"start": v(488.95, 1187.45) * mm, "end": v(469.9, 1187.45) * mm});
            skLineSegment(sketch, "E10.2.8.0", {"start": v(488.95, 1314.45) * mm, "end": v(488.95, 1295.4) * mm});
            skLineSegment(sketch, "E10.2.8.1", {"start": v(469.9, 1314.45) * mm, "end": v(469.9, 1295.4) * mm});
            skLineSegment(sketch, "E10.2.8.2", {"start": v(488.95, 1295.4) * mm, "end": v(469.9, 1295.4) * mm});
            skLineSegment(sketch, "E10.2.8.3", {"start": v(488.95, 1314.45) * mm, "end": v(469.9, 1314.45) * mm});
            skLineSegment(sketch, "E10.2.9.0", {"start": v(488.95, 1441.45) * mm, "end": v(488.95, 1422.4) * mm});
            skLineSegment(sketch, "E10.2.9.1", {"start": v(469.9, 1441.45) * mm, "end": v(469.9, 1422.4) * mm});
            skLineSegment(sketch, "E10.2.9.2", {"start": v(488.95, 1422.4) * mm, "end": v(469.9, 1422.4) * mm});
            skLineSegment(sketch, "E10.2.9.3", {"start": v(488.95, 1441.45) * mm, "end": v(469.9, 1441.45) * mm});
            skLineSegment(sketch, "E10.direction1", {"start": v(177.8, 279.4) * mm, "end": v(323.85, 279.4) * mm, "construction": true});
            skLineSegment(sketch, "E10.direction2", {"start": v(177.8, 279.4) * mm, "end": v(177.8, 406.4) * mm, "construction": true});
            skLineSegment(sketch, "E11.0.3.0", {"start": v(635, 298.45) * mm, "end": v(635, 279.4) * mm});
            skLineSegment(sketch, "E11.3.3.0", {"start": v(615.95, 298.45) * mm, "end": v(615.95, 279.4) * mm});
            skLineSegment(sketch, "E11.6.3.0", {"start": v(635, 279.4) * mm, "end": v(615.95, 279.4) * mm});
            skLineSegment(sketch, "E11.9.3.0", {"start": v(635, 298.45) * mm, "end": v(615.95, 298.45) * mm});
            skLineSegment(sketch, "E11.0.3.1", {"start": v(635, 425.45) * mm, "end": v(635, 406.4) * mm});
            skLineSegment(sketch, "E11.3.3.1", {"start": v(615.95, 425.45) * mm, "end": v(615.95, 406.4) * mm});
            skLineSegment(sketch, "E11.6.3.1", {"start": v(635, 406.4) * mm, "end": v(615.95, 406.4) * mm});
            skLineSegment(sketch, "E11.9.3.1", {"start": v(635, 425.45) * mm, "end": v(615.95, 425.45) * mm});
            skLineSegment(sketch, "E11.0.3.2", {"start": v(635, 552.45) * mm, "end": v(635, 533.4) * mm});
            skLineSegment(sketch, "E11.3.3.2", {"start": v(615.95, 552.45) * mm, "end": v(615.95, 533.4) * mm});
            skLineSegment(sketch, "E11.6.3.2", {"start": v(635, 533.4) * mm, "end": v(615.95, 533.4) * mm});
            skLineSegment(sketch, "E11.9.3.2", {"start": v(635, 552.45) * mm, "end": v(615.95, 552.45) * mm});
            skLineSegment(sketch, "E11.0.3.3", {"start": v(635, 679.45) * mm, "end": v(635, 660.4) * mm});
            skLineSegment(sketch, "E11.3.3.3", {"start": v(615.95, 679.45) * mm, "end": v(615.95, 660.4) * mm});
            skLineSegment(sketch, "E11.6.3.3", {"start": v(635, 660.4) * mm, "end": v(615.95, 660.4) * mm});
            skLineSegment(sketch, "E11.9.3.3", {"start": v(635, 679.45) * mm, "end": v(615.95, 679.45) * mm});
            skLineSegment(sketch, "E11.0.3.4", {"start": v(635, 806.45) * mm, "end": v(635, 787.4) * mm});
            skLineSegment(sketch, "E11.3.3.4", {"start": v(615.95, 806.45) * mm, "end": v(615.95, 787.4) * mm});
            skLineSegment(sketch, "E11.6.3.4", {"start": v(635, 787.4) * mm, "end": v(615.95, 787.4) * mm});
            skLineSegment(sketch, "E11.9.3.4", {"start": v(635, 806.45) * mm, "end": v(615.95, 806.45) * mm});
            skLineSegment(sketch, "E11.0.3.5", {"start": v(635, 933.45) * mm, "end": v(635, 914.4) * mm});
            skLineSegment(sketch, "E11.3.3.5", {"start": v(615.95, 933.45) * mm, "end": v(615.95, 914.4) * mm});
            skLineSegment(sketch, "E11.6.3.5", {"start": v(635, 914.4) * mm, "end": v(615.95, 914.4) * mm});
            skLineSegment(sketch, "E11.9.3.5", {"start": v(635, 933.45) * mm, "end": v(615.95, 933.45) * mm});
            skLineSegment(sketch, "E11.0.3.6", {"start": v(635, 1060.45) * mm, "end": v(635, 1041.4) * mm});
            skLineSegment(sketch, "E11.3.3.6", {"start": v(615.95, 1060.45) * mm, "end": v(615.95, 1041.4) * mm});
            skLineSegment(sketch, "E11.6.3.6", {"start": v(635, 1041.4) * mm, "end": v(615.95, 1041.4) * mm});
            skLineSegment(sketch, "E11.9.3.6", {"start": v(635, 1060.45) * mm, "end": v(615.95, 1060.45) * mm});
            skLineSegment(sketch, "E11.0.3.7", {"start": v(635, 1187.45) * mm, "end": v(635, 1168.4) * mm});
            skLineSegment(sketch, "E11.3.3.7", {"start": v(615.95, 1187.45) * mm, "end": v(615.95, 1168.4) * mm});
            skLineSegment(sketch, "E11.6.3.7", {"start": v(635, 1168.4) * mm, "end": v(615.95, 1168.4) * mm});
            skLineSegment(sketch, "E11.9.3.7", {"start": v(635, 1187.45) * mm, "end": v(615.95, 1187.45) * mm});
            skLineSegment(sketch, "E11.0.3.8", {"start": v(635, 1314.45) * mm, "end": v(635, 1295.4) * mm});
            skLineSegment(sketch, "E11.3.3.8", {"start": v(615.95, 1314.45) * mm, "end": v(615.95, 1295.4) * mm});
            skLineSegment(sketch, "E11.6.3.8", {"start": v(635, 1295.4) * mm, "end": v(615.95, 1295.4) * mm});
            skLineSegment(sketch, "E11.9.3.8", {"start": v(635, 1314.45) * mm, "end": v(615.95, 1314.45) * mm});
            skLineSegment(sketch, "E11.0.3.9", {"start": v(635, 1441.45) * mm, "end": v(635, 1422.4) * mm});
            skLineSegment(sketch, "E11.3.3.9", {"start": v(615.95, 1441.45) * mm, "end": v(615.95, 1422.4) * mm});
            skLineSegment(sketch, "E11.6.3.9", {"start": v(635, 1422.4) * mm, "end": v(615.95, 1422.4) * mm});
            skLineSegment(sketch, "E11.9.3.9", {"start": v(635, 1441.45) * mm, "end": v(615.95, 1441.45) * mm});
            skLineSegment(sketch, "E11.0.4.0", {"start": v(781.05, 298.45) * mm, "end": v(781.05, 279.4) * mm});
            skLineSegment(sketch, "E11.3.4.0", {"start": v(762, 298.45) * mm, "end": v(762, 279.4) * mm});
            skLineSegment(sketch, "E11.6.4.0", {"start": v(781.05, 279.4) * mm, "end": v(762, 279.4) * mm});
            skLineSegment(sketch, "E11.9.4.0", {"start": v(781.05, 298.45) * mm, "end": v(762, 298.45) * mm});
            skLineSegment(sketch, "E11.0.4.1", {"start": v(781.05, 425.45) * mm, "end": v(781.05, 406.4) * mm});
            skLineSegment(sketch, "E11.3.4.1", {"start": v(762, 425.45) * mm, "end": v(762, 406.4) * mm});
            skLineSegment(sketch, "E11.6.4.1", {"start": v(781.05, 406.4) * mm, "end": v(762, 406.4) * mm});
            skLineSegment(sketch, "E11.9.4.1", {"start": v(781.05, 425.45) * mm, "end": v(762, 425.45) * mm});
            skLineSegment(sketch, "E11.0.4.2", {"start": v(781.05, 552.45) * mm, "end": v(781.05, 533.4) * mm});
            skLineSegment(sketch, "E11.3.4.2", {"start": v(762, 552.45) * mm, "end": v(762, 533.4) * mm});
            skLineSegment(sketch, "E11.6.4.2", {"start": v(781.05, 533.4) * mm, "end": v(762, 533.4) * mm});
            skLineSegment(sketch, "E11.9.4.2", {"start": v(781.05, 552.45) * mm, "end": v(762, 552.45) * mm});
            skLineSegment(sketch, "E11.0.4.3", {"start": v(781.05, 679.45) * mm, "end": v(781.05, 660.4) * mm});
            skLineSegment(sketch, "E11.3.4.3", {"start": v(762, 679.45) * mm, "end": v(762, 660.4) * mm});
            skLineSegment(sketch, "E11.6.4.3", {"start": v(781.05, 660.4) * mm, "end": v(762, 660.4) * mm});
            skLineSegment(sketch, "E11.9.4.3", {"start": v(781.05, 679.45) * mm, "end": v(762, 679.45) * mm});
            skLineSegment(sketch, "E11.0.4.4", {"start": v(781.05, 806.45) * mm, "end": v(781.05, 787.4) * mm});
            skLineSegment(sketch, "E11.3.4.4", {"start": v(762, 806.45) * mm, "end": v(762, 787.4) * mm});
            skLineSegment(sketch, "E11.6.4.4", {"start": v(781.05, 787.4) * mm, "end": v(762, 787.4) * mm});
            skLineSegment(sketch, "E11.9.4.4", {"start": v(781.05, 806.45) * mm, "end": v(762, 806.45) * mm});
            skLineSegment(sketch, "E11.0.4.5", {"start": v(781.05, 933.45) * mm, "end": v(781.05, 914.4) * mm});
            skLineSegment(sketch, "E11.3.4.5", {"start": v(762, 933.45) * mm, "end": v(762, 914.4) * mm});
            skLineSegment(sketch, "E11.6.4.5", {"start": v(781.05, 914.4) * mm, "end": v(762, 914.4) * mm});
            skLineSegment(sketch, "E11.9.4.5", {"start": v(781.05, 933.45) * mm, "end": v(762, 933.45) * mm});
            skLineSegment(sketch, "E11.0.4.6", {"start": v(781.05, 1060.45) * mm, "end": v(781.05, 1041.4) * mm});
            skLineSegment(sketch, "E11.3.4.6", {"start": v(762, 1060.45) * mm, "end": v(762, 1041.4) * mm});
            skLineSegment(sketch, "E11.6.4.6", {"start": v(781.05, 1041.4) * mm, "end": v(762, 1041.4) * mm});
            skLineSegment(sketch, "E11.9.4.6", {"start": v(781.05, 1060.45) * mm, "end": v(762, 1060.45) * mm});
            skLineSegment(sketch, "E11.0.4.7", {"start": v(781.05, 1187.45) * mm, "end": v(781.05, 1168.4) * mm});
            skLineSegment(sketch, "E11.3.4.7", {"start": v(762, 1187.45) * mm, "end": v(762, 1168.4) * mm});
            skLineSegment(sketch, "E11.6.4.7", {"start": v(781.05, 1168.4) * mm, "end": v(762, 1168.4) * mm});
            skLineSegment(sketch, "E11.9.4.7", {"start": v(781.05, 1187.45) * mm, "end": v(762, 1187.45) * mm});
            skLineSegment(sketch, "E11.0.4.8", {"start": v(781.05, 1314.45) * mm, "end": v(781.05, 1295.4) * mm});
            skLineSegment(sketch, "E11.3.4.8", {"start": v(762, 1314.45) * mm, "end": v(762, 1295.4) * mm});
            skLineSegment(sketch, "E11.6.4.8", {"start": v(781.05, 1295.4) * mm, "end": v(762, 1295.4) * mm});
            skLineSegment(sketch, "E11.9.4.8", {"start": v(781.05, 1314.45) * mm, "end": v(762, 1314.45) * mm});
            skLineSegment(sketch, "E11.0.4.9", {"start": v(781.05, 1441.45) * mm, "end": v(781.05, 1422.4) * mm});
            skLineSegment(sketch, "E11.3.4.9", {"start": v(762, 1441.45) * mm, "end": v(762, 1422.4) * mm});
            skLineSegment(sketch, "E11.6.4.9", {"start": v(781.05, 1422.4) * mm, "end": v(762, 1422.4) * mm});
            skLineSegment(sketch, "E11.9.4.9", {"start": v(781.05, 1441.45) * mm, "end": v(762, 1441.45) * mm});
            skLineSegment(sketch, "E11.0.5.0", {"start": v(927.1, 298.45) * mm, "end": v(927.1, 279.4) * mm});
            skLineSegment(sketch, "E11.3.5.0", {"start": v(908.05, 298.45) * mm, "end": v(908.05, 279.4) * mm});
            skLineSegment(sketch, "E11.6.5.0", {"start": v(927.1, 279.4) * mm, "end": v(908.05, 279.4) * mm});
            skLineSegment(sketch, "E11.9.5.0", {"start": v(927.1, 298.45) * mm, "end": v(908.05, 298.45) * mm});
            skLineSegment(sketch, "E11.0.5.1", {"start": v(927.1, 425.45) * mm, "end": v(927.1, 406.4) * mm});
            skLineSegment(sketch, "E11.3.5.1", {"start": v(908.05, 425.45) * mm, "end": v(908.05, 406.4) * mm});
            skLineSegment(sketch, "E11.6.5.1", {"start": v(927.1, 406.4) * mm, "end": v(908.05, 406.4) * mm});
            skLineSegment(sketch, "E11.9.5.1", {"start": v(927.1, 425.45) * mm, "end": v(908.05, 425.45) * mm});
            skLineSegment(sketch, "E11.0.5.2", {"start": v(927.1, 552.45) * mm, "end": v(927.1, 533.4) * mm});
            skLineSegment(sketch, "E11.3.5.2", {"start": v(908.05, 552.45) * mm, "end": v(908.05, 533.4) * mm});
            skLineSegment(sketch, "E11.6.5.2", {"start": v(927.1, 533.4) * mm, "end": v(908.05, 533.4) * mm});
            skLineSegment(sketch, "E11.9.5.2", {"start": v(927.1, 552.45) * mm, "end": v(908.05, 552.45) * mm});
            skLineSegment(sketch, "E11.0.5.3", {"start": v(927.1, 679.45) * mm, "end": v(927.1, 660.4) * mm});
            skLineSegment(sketch, "E11.3.5.3", {"start": v(908.05, 679.45) * mm, "end": v(908.05, 660.4) * mm});
            skLineSegment(sketch, "E11.6.5.3", {"start": v(927.1, 660.4) * mm, "end": v(908.05, 660.4) * mm});
            skLineSegment(sketch, "E11.9.5.3", {"start": v(927.1, 679.45) * mm, "end": v(908.05, 679.45) * mm});
            skLineSegment(sketch, "E11.0.5.4", {"start": v(927.1, 806.45) * mm, "end": v(927.1, 787.4) * mm});
            skLineSegment(sketch, "E11.3.5.4", {"start": v(908.05, 806.45) * mm, "end": v(908.05, 787.4) * mm});
            skLineSegment(sketch, "E11.6.5.4", {"start": v(927.1, 787.4) * mm, "end": v(908.05, 787.4) * mm});
            skLineSegment(sketch, "E11.9.5.4", {"start": v(927.1, 806.45) * mm, "end": v(908.05, 806.45) * mm});
            skLineSegment(sketch, "E11.0.5.5", {"start": v(927.1, 933.45) * mm, "end": v(927.1, 914.4) * mm});
            skLineSegment(sketch, "E11.3.5.5", {"start": v(908.05, 933.45) * mm, "end": v(908.05, 914.4) * mm});
            skLineSegment(sketch, "E11.6.5.5", {"start": v(927.1, 914.4) * mm, "end": v(908.05, 914.4) * mm});
            skLineSegment(sketch, "E11.9.5.5", {"start": v(927.1, 933.45) * mm, "end": v(908.05, 933.45) * mm});
            skLineSegment(sketch, "E11.0.5.6", {"start": v(927.1, 1060.45) * mm, "end": v(927.1, 1041.4) * mm});
            skLineSegment(sketch, "E11.3.5.6", {"start": v(908.05, 1060.45) * mm, "end": v(908.05, 1041.4) * mm});
            skLineSegment(sketch, "E11.6.5.6", {"start": v(927.1, 1041.4) * mm, "end": v(908.05, 1041.4) * mm});
            skLineSegment(sketch, "E11.9.5.6", {"start": v(927.1, 1060.45) * mm, "end": v(908.05, 1060.45) * mm});
            skLineSegment(sketch, "E11.0.5.7", {"start": v(927.1, 1187.45) * mm, "end": v(927.1, 1168.4) * mm});
            skLineSegment(sketch, "E11.3.5.7", {"start": v(908.05, 1187.45) * mm, "end": v(908.05, 1168.4) * mm});
            skLineSegment(sketch, "E11.6.5.7", {"start": v(927.1, 1168.4) * mm, "end": v(908.05, 1168.4) * mm});
            skLineSegment(sketch, "E11.9.5.7", {"start": v(927.1, 1187.45) * mm, "end": v(908.05, 1187.45) * mm});
            skLineSegment(sketch, "E11.0.5.8", {"start": v(927.1, 1314.45) * mm, "end": v(927.1, 1295.4) * mm});
            skLineSegment(sketch, "E11.3.5.8", {"start": v(908.05, 1314.45) * mm, "end": v(908.05, 1295.4) * mm});
            skLineSegment(sketch, "E11.6.5.8", {"start": v(927.1, 1295.4) * mm, "end": v(908.05, 1295.4) * mm});
            skLineSegment(sketch, "E11.9.5.8", {"start": v(927.1, 1314.45) * mm, "end": v(908.05, 1314.45) * mm});
            skLineSegment(sketch, "E11.0.5.9", {"start": v(927.1, 1441.45) * mm, "end": v(927.1, 1422.4) * mm});
            skLineSegment(sketch, "E11.3.5.9", {"start": v(908.05, 1441.45) * mm, "end": v(908.05, 1422.4) * mm});
            skLineSegment(sketch, "E11.6.5.9", {"start": v(927.1, 1422.4) * mm, "end": v(908.05, 1422.4) * mm});
            skLineSegment(sketch, "E11.9.5.9", {"start": v(927.1, 1441.45) * mm, "end": v(908.05, 1441.45) * mm});
            skLineSegment(sketch, "E11.0.6.0", {"start": v(1073.15, 298.45) * mm, "end": v(1073.15, 279.4) * mm});
            skLineSegment(sketch, "E11.3.6.0", {"start": v(1054.1, 298.45) * mm, "end": v(1054.1, 279.4) * mm});
            skLineSegment(sketch, "E11.6.6.0", {"start": v(1073.15, 279.4) * mm, "end": v(1054.1, 279.4) * mm});
            skLineSegment(sketch, "E11.9.6.0", {"start": v(1073.15, 298.45) * mm, "end": v(1054.1, 298.45) * mm});
            skLineSegment(sketch, "E11.0.6.1", {"start": v(1073.15, 425.45) * mm, "end": v(1073.15, 406.4) * mm});
            skLineSegment(sketch, "E11.3.6.1", {"start": v(1054.1, 425.45) * mm, "end": v(1054.1, 406.4) * mm});
            skLineSegment(sketch, "E11.6.6.1", {"start": v(1073.15, 406.4) * mm, "end": v(1054.1, 406.4) * mm});
            skLineSegment(sketch, "E11.9.6.1", {"start": v(1073.15, 425.45) * mm, "end": v(1054.1, 425.45) * mm});
            skLineSegment(sketch, "E11.0.6.2", {"start": v(1073.15, 552.45) * mm, "end": v(1073.15, 533.4) * mm});
            skLineSegment(sketch, "E11.3.6.2", {"start": v(1054.1, 552.45) * mm, "end": v(1054.1, 533.4) * mm});
            skLineSegment(sketch, "E11.6.6.2", {"start": v(1073.15, 533.4) * mm, "end": v(1054.1, 533.4) * mm});
            skLineSegment(sketch, "E11.9.6.2", {"start": v(1073.15, 552.45) * mm, "end": v(1054.1, 552.45) * mm});
            skLineSegment(sketch, "E11.0.6.3", {"start": v(1073.15, 679.45) * mm, "end": v(1073.15, 660.4) * mm});
            skLineSegment(sketch, "E11.3.6.3", {"start": v(1054.1, 679.45) * mm, "end": v(1054.1, 660.4) * mm});
            skLineSegment(sketch, "E11.6.6.3", {"start": v(1073.15, 660.4) * mm, "end": v(1054.1, 660.4) * mm});
            skLineSegment(sketch, "E11.9.6.3", {"start": v(1073.15, 679.45) * mm, "end": v(1054.1, 679.45) * mm});
            skLineSegment(sketch, "E11.0.6.4", {"start": v(1073.15, 806.45) * mm, "end": v(1073.15, 787.4) * mm});
            skLineSegment(sketch, "E11.3.6.4", {"start": v(1054.1, 806.45) * mm, "end": v(1054.1, 787.4) * mm});
            skLineSegment(sketch, "E11.6.6.4", {"start": v(1073.15, 787.4) * mm, "end": v(1054.1, 787.4) * mm});
            skLineSegment(sketch, "E11.9.6.4", {"start": v(1073.15, 806.45) * mm, "end": v(1054.1, 806.45) * mm});
            skLineSegment(sketch, "E11.0.6.5", {"start": v(1073.15, 933.45) * mm, "end": v(1073.15, 914.4) * mm});
            skLineSegment(sketch, "E11.3.6.5", {"start": v(1054.1, 933.45) * mm, "end": v(1054.1, 914.4) * mm});
            skLineSegment(sketch, "E11.6.6.5", {"start": v(1073.15, 914.4) * mm, "end": v(1054.1, 914.4) * mm});
            skLineSegment(sketch, "E11.9.6.5", {"start": v(1073.15, 933.45) * mm, "end": v(1054.1, 933.45) * mm});
            skLineSegment(sketch, "E11.0.6.6", {"start": v(1073.15, 1060.45) * mm, "end": v(1073.15, 1041.4) * mm});
            skLineSegment(sketch, "E11.3.6.6", {"start": v(1054.1, 1060.45) * mm, "end": v(1054.1, 1041.4) * mm});
            skLineSegment(sketch, "E11.6.6.6", {"start": v(1073.15, 1041.4) * mm, "end": v(1054.1, 1041.4) * mm});
            skLineSegment(sketch, "E11.9.6.6", {"start": v(1073.15, 1060.45) * mm, "end": v(1054.1, 1060.45) * mm});
            skLineSegment(sketch, "E11.0.6.7", {"start": v(1073.15, 1187.45) * mm, "end": v(1073.15, 1168.4) * mm});
            skLineSegment(sketch, "E11.3.6.7", {"start": v(1054.1, 1187.45) * mm, "end": v(1054.1, 1168.4) * mm});
            skLineSegment(sketch, "E11.6.6.7", {"start": v(1073.15, 1168.4) * mm, "end": v(1054.1, 1168.4) * mm});
            skLineSegment(sketch, "E11.9.6.7", {"start": v(1073.15, 1187.45) * mm, "end": v(1054.1, 1187.45) * mm});
            skLineSegment(sketch, "E11.0.6.8", {"start": v(1073.15, 1314.45) * mm, "end": v(1073.15, 1295.4) * mm});
            skLineSegment(sketch, "E11.3.6.8", {"start": v(1054.1, 1314.45) * mm, "end": v(1054.1, 1295.4) * mm});
            skLineSegment(sketch, "E11.6.6.8", {"start": v(1073.15, 1295.4) * mm, "end": v(1054.1, 1295.4) * mm});
            skLineSegment(sketch, "E11.9.6.8", {"start": v(1073.15, 1314.45) * mm, "end": v(1054.1, 1314.45) * mm});
            skLineSegment(sketch, "E11.0.6.9", {"start": v(1073.15, 1441.45) * mm, "end": v(1073.15, 1422.4) * mm});
            skLineSegment(sketch, "E11.3.6.9", {"start": v(1054.1, 1441.45) * mm, "end": v(1054.1, 1422.4) * mm});
            skLineSegment(sketch, "E11.6.6.9", {"start": v(1073.15, 1422.4) * mm, "end": v(1054.1, 1422.4) * mm});
            skLineSegment(sketch, "E11.9.6.9", {"start": v(1073.15, 1441.45) * mm, "end": v(1054.1, 1441.45) * mm});
            skLineSegment(sketch, "E11.0.7.0", {"start": v(1219.2, 298.45) * mm, "end": v(1219.2, 279.4) * mm});
            skLineSegment(sketch, "E11.3.7.0", {"start": v(1200.15, 298.45) * mm, "end": v(1200.15, 279.4) * mm});
            skLineSegment(sketch, "E11.6.7.0", {"start": v(1219.2, 279.4) * mm, "end": v(1200.15, 279.4) * mm});
            skLineSegment(sketch, "E11.9.7.0", {"start": v(1219.2, 298.45) * mm, "end": v(1200.15, 298.45) * mm});
            skLineSegment(sketch, "E11.0.7.1", {"start": v(1219.2, 425.45) * mm, "end": v(1219.2, 406.4) * mm});
            skLineSegment(sketch, "E11.3.7.1", {"start": v(1200.15, 425.45) * mm, "end": v(1200.15, 406.4) * mm});
            skLineSegment(sketch, "E11.6.7.1", {"start": v(1219.2, 406.4) * mm, "end": v(1200.15, 406.4) * mm});
            skLineSegment(sketch, "E11.9.7.1", {"start": v(1219.2, 425.45) * mm, "end": v(1200.15, 425.45) * mm});
            skLineSegment(sketch, "E11.0.7.2", {"start": v(1219.2, 552.45) * mm, "end": v(1219.2, 533.4) * mm});
            skLineSegment(sketch, "E11.3.7.2", {"start": v(1200.15, 552.45) * mm, "end": v(1200.15, 533.4) * mm});
            skLineSegment(sketch, "E11.6.7.2", {"start": v(1219.2, 533.4) * mm, "end": v(1200.15, 533.4) * mm});
            skLineSegment(sketch, "E11.9.7.2", {"start": v(1219.2, 552.45) * mm, "end": v(1200.15, 552.45) * mm});
            skLineSegment(sketch, "E11.0.7.3", {"start": v(1219.2, 679.45) * mm, "end": v(1219.2, 660.4) * mm});
            skLineSegment(sketch, "E11.3.7.3", {"start": v(1200.15, 679.45) * mm, "end": v(1200.15, 660.4) * mm});
            skLineSegment(sketch, "E11.6.7.3", {"start": v(1219.2, 660.4) * mm, "end": v(1200.15, 660.4) * mm});
            skLineSegment(sketch, "E11.9.7.3", {"start": v(1219.2, 679.45) * mm, "end": v(1200.15, 679.45) * mm});
            skLineSegment(sketch, "E11.0.7.4", {"start": v(1219.2, 806.45) * mm, "end": v(1219.2, 787.4) * mm});
            skLineSegment(sketch, "E11.3.7.4", {"start": v(1200.15, 806.45) * mm, "end": v(1200.15, 787.4) * mm});
            skLineSegment(sketch, "E11.6.7.4", {"start": v(1219.2, 787.4) * mm, "end": v(1200.15, 787.4) * mm});
            skLineSegment(sketch, "E11.9.7.4", {"start": v(1219.2, 806.45) * mm, "end": v(1200.15, 806.45) * mm});
            skLineSegment(sketch, "E11.0.7.5", {"start": v(1219.2, 933.45) * mm, "end": v(1219.2, 914.4) * mm});
            skLineSegment(sketch, "E11.3.7.5", {"start": v(1200.15, 933.45) * mm, "end": v(1200.15, 914.4) * mm});
            skLineSegment(sketch, "E11.6.7.5", {"start": v(1219.2, 914.4) * mm, "end": v(1200.15, 914.4) * mm});
            skLineSegment(sketch, "E11.9.7.5", {"start": v(1219.2, 933.45) * mm, "end": v(1200.15, 933.45) * mm});
            skLineSegment(sketch, "E11.0.7.6", {"start": v(1219.2, 1060.45) * mm, "end": v(1219.2, 1041.4) * mm});
            skLineSegment(sketch, "E11.3.7.6", {"start": v(1200.15, 1060.45) * mm, "end": v(1200.15, 1041.4) * mm});
            skLineSegment(sketch, "E11.6.7.6", {"start": v(1219.2, 1041.4) * mm, "end": v(1200.15, 1041.4) * mm});
            skLineSegment(sketch, "E11.9.7.6", {"start": v(1219.2, 1060.45) * mm, "end": v(1200.15, 1060.45) * mm});
            skLineSegment(sketch, "E11.0.7.7", {"start": v(1219.2, 1187.45) * mm, "end": v(1219.2, 1168.4) * mm});
            skLineSegment(sketch, "E11.3.7.7", {"start": v(1200.15, 1187.45) * mm, "end": v(1200.15, 1168.4) * mm});
            skLineSegment(sketch, "E11.6.7.7", {"start": v(1219.2, 1168.4) * mm, "end": v(1200.15, 1168.4) * mm});
            skLineSegment(sketch, "E11.9.7.7", {"start": v(1219.2, 1187.45) * mm, "end": v(1200.15, 1187.45) * mm});
            skLineSegment(sketch, "E11.0.7.8", {"start": v(1219.2, 1314.45) * mm, "end": v(1219.2, 1295.4) * mm});
            skLineSegment(sketch, "E11.3.7.8", {"start": v(1200.15, 1314.45) * mm, "end": v(1200.15, 1295.4) * mm});
            skLineSegment(sketch, "E11.6.7.8", {"start": v(1219.2, 1295.4) * mm, "end": v(1200.15, 1295.4) * mm});
            skLineSegment(sketch, "E11.9.7.8", {"start": v(1219.2, 1314.45) * mm, "end": v(1200.15, 1314.45) * mm});
            skLineSegment(sketch, "E11.0.7.9", {"start": v(1219.2, 1441.45) * mm, "end": v(1219.2, 1422.4) * mm});
            skLineSegment(sketch, "E11.3.7.9", {"start": v(1200.15, 1441.45) * mm, "end": v(1200.15, 1422.4) * mm});
            skLineSegment(sketch, "E11.6.7.9", {"start": v(1219.2, 1422.4) * mm, "end": v(1200.15, 1422.4) * mm});
            skLineSegment(sketch, "E11.9.7.9", {"start": v(1219.2, 1441.45) * mm, "end": v(1200.15, 1441.45) * mm});
            skLineSegment(sketch, "E11.0.8.0", {"start": v(1365.25, 298.45) * mm, "end": v(1365.25, 279.4) * mm});
            skLineSegment(sketch, "E11.3.8.0", {"start": v(1346.2, 298.45) * mm, "end": v(1346.2, 279.4) * mm});
            skLineSegment(sketch, "E11.6.8.0", {"start": v(1365.25, 279.4) * mm, "end": v(1346.2, 279.4) * mm});
            skLineSegment(sketch, "E11.9.8.0", {"start": v(1365.25, 298.45) * mm, "end": v(1346.2, 298.45) * mm});
            skLineSegment(sketch, "E11.0.8.1", {"start": v(1365.25, 425.45) * mm, "end": v(1365.25, 406.4) * mm});
            skLineSegment(sketch, "E11.3.8.1", {"start": v(1346.2, 425.45) * mm, "end": v(1346.2, 406.4) * mm});
            skLineSegment(sketch, "E11.6.8.1", {"start": v(1365.25, 406.4) * mm, "end": v(1346.2, 406.4) * mm});
            skLineSegment(sketch, "E11.9.8.1", {"start": v(1365.25, 425.45) * mm, "end": v(1346.2, 425.45) * mm});
            skLineSegment(sketch, "E11.0.8.2", {"start": v(1365.25, 552.45) * mm, "end": v(1365.25, 533.4) * mm});
            skLineSegment(sketch, "E11.3.8.2", {"start": v(1346.2, 552.45) * mm, "end": v(1346.2, 533.4) * mm});
            skLineSegment(sketch, "E11.6.8.2", {"start": v(1365.25, 533.4) * mm, "end": v(1346.2, 533.4) * mm});
            skLineSegment(sketch, "E11.9.8.2", {"start": v(1365.25, 552.45) * mm, "end": v(1346.2, 552.45) * mm});
            skLineSegment(sketch, "E11.0.8.3", {"start": v(1365.25, 679.45) * mm, "end": v(1365.25, 660.4) * mm});
            skLineSegment(sketch, "E11.3.8.3", {"start": v(1346.2, 679.45) * mm, "end": v(1346.2, 660.4) * mm});
            skLineSegment(sketch, "E11.6.8.3", {"start": v(1365.25, 660.4) * mm, "end": v(1346.2, 660.4) * mm});
            skLineSegment(sketch, "E11.9.8.3", {"start": v(1365.25, 679.45) * mm, "end": v(1346.2, 679.45) * mm});
            skLineSegment(sketch, "E11.0.8.4", {"start": v(1365.25, 806.45) * mm, "end": v(1365.25, 787.4) * mm});
            skLineSegment(sketch, "E11.3.8.4", {"start": v(1346.2, 806.45) * mm, "end": v(1346.2, 787.4) * mm});
            skLineSegment(sketch, "E11.6.8.4", {"start": v(1365.25, 787.4) * mm, "end": v(1346.2, 787.4) * mm});
            skLineSegment(sketch, "E11.9.8.4", {"start": v(1365.25, 806.45) * mm, "end": v(1346.2, 806.45) * mm});
            skLineSegment(sketch, "E11.0.8.5", {"start": v(1365.25, 933.45) * mm, "end": v(1365.25, 914.4) * mm});
            skLineSegment(sketch, "E11.3.8.5", {"start": v(1346.2, 933.45) * mm, "end": v(1346.2, 914.4) * mm});
            skLineSegment(sketch, "E11.6.8.5", {"start": v(1365.25, 914.4) * mm, "end": v(1346.2, 914.4) * mm});
            skLineSegment(sketch, "E11.9.8.5", {"start": v(1365.25, 933.45) * mm, "end": v(1346.2, 933.45) * mm});
            skLineSegment(sketch, "E11.0.8.6", {"start": v(1365.25, 1060.45) * mm, "end": v(1365.25, 1041.4) * mm});
            skLineSegment(sketch, "E11.3.8.6", {"start": v(1346.2, 1060.45) * mm, "end": v(1346.2, 1041.4) * mm});
            skLineSegment(sketch, "E11.6.8.6", {"start": v(1365.25, 1041.4) * mm, "end": v(1346.2, 1041.4) * mm});
            skLineSegment(sketch, "E11.9.8.6", {"start": v(1365.25, 1060.45) * mm, "end": v(1346.2, 1060.45) * mm});
            skLineSegment(sketch, "E11.0.8.7", {"start": v(1365.25, 1187.45) * mm, "end": v(1365.25, 1168.4) * mm});
            skLineSegment(sketch, "E11.3.8.7", {"start": v(1346.2, 1187.45) * mm, "end": v(1346.2, 1168.4) * mm});
            skLineSegment(sketch, "E11.6.8.7", {"start": v(1365.25, 1168.4) * mm, "end": v(1346.2, 1168.4) * mm});
            skLineSegment(sketch, "E11.9.8.7", {"start": v(1365.25, 1187.45) * mm, "end": v(1346.2, 1187.45) * mm});
            skLineSegment(sketch, "E11.0.8.8", {"start": v(1365.25, 1314.45) * mm, "end": v(1365.25, 1295.4) * mm});
            skLineSegment(sketch, "E11.3.8.8", {"start": v(1346.2, 1314.45) * mm, "end": v(1346.2, 1295.4) * mm});
            skLineSegment(sketch, "E11.6.8.8", {"start": v(1365.25, 1295.4) * mm, "end": v(1346.2, 1295.4) * mm});
            skLineSegment(sketch, "E11.9.8.8", {"start": v(1365.25, 1314.45) * mm, "end": v(1346.2, 1314.45) * mm});
            skLineSegment(sketch, "E11.0.8.9", {"start": v(1365.25, 1441.45) * mm, "end": v(1365.25, 1422.4) * mm});
            skLineSegment(sketch, "E11.3.8.9", {"start": v(1346.2, 1441.45) * mm, "end": v(1346.2, 1422.4) * mm});
            skLineSegment(sketch, "E11.6.8.9", {"start": v(1365.25, 1422.4) * mm, "end": v(1346.2, 1422.4) * mm});
            skLineSegment(sketch, "E11.9.8.9", {"start": v(1365.25, 1441.45) * mm, "end": v(1346.2, 1441.45) * mm});
            skLineSegment(sketch, "E11.0.9.0", {"start": v(1511.3, 298.45) * mm, "end": v(1511.3, 279.4) * mm});
            skLineSegment(sketch, "E11.3.9.0", {"start": v(1492.25, 298.45) * mm, "end": v(1492.25, 279.4) * mm});
            skLineSegment(sketch, "E11.6.9.0", {"start": v(1511.3, 279.4) * mm, "end": v(1492.25, 279.4) * mm});
            skLineSegment(sketch, "E11.9.9.0", {"start": v(1511.3, 298.45) * mm, "end": v(1492.25, 298.45) * mm});
            skLineSegment(sketch, "E11.0.9.1", {"start": v(1511.3, 425.45) * mm, "end": v(1511.3, 406.4) * mm});
            skLineSegment(sketch, "E11.3.9.1", {"start": v(1492.25, 425.45) * mm, "end": v(1492.25, 406.4) * mm});
            skLineSegment(sketch, "E11.6.9.1", {"start": v(1511.3, 406.4) * mm, "end": v(1492.25, 406.4) * mm});
            skLineSegment(sketch, "E11.9.9.1", {"start": v(1511.3, 425.45) * mm, "end": v(1492.25, 425.45) * mm});
            skLineSegment(sketch, "E11.0.9.2", {"start": v(1511.3, 552.45) * mm, "end": v(1511.3, 533.4) * mm});
            skLineSegment(sketch, "E11.3.9.2", {"start": v(1492.25, 552.45) * mm, "end": v(1492.25, 533.4) * mm});
            skLineSegment(sketch, "E11.6.9.2", {"start": v(1511.3, 533.4) * mm, "end": v(1492.25, 533.4) * mm});
            skLineSegment(sketch, "E11.9.9.2", {"start": v(1511.3, 552.45) * mm, "end": v(1492.25, 552.45) * mm});
            skLineSegment(sketch, "E11.0.9.3", {"start": v(1511.3, 679.45) * mm, "end": v(1511.3, 660.4) * mm});
            skLineSegment(sketch, "E11.3.9.3", {"start": v(1492.25, 679.45) * mm, "end": v(1492.25, 660.4) * mm});
            skLineSegment(sketch, "E11.6.9.3", {"start": v(1511.3, 660.4) * mm, "end": v(1492.25, 660.4) * mm});
            skLineSegment(sketch, "E11.9.9.3", {"start": v(1511.3, 679.45) * mm, "end": v(1492.25, 679.45) * mm});
            skLineSegment(sketch, "E11.0.9.4", {"start": v(1511.3, 806.45) * mm, "end": v(1511.3, 787.4) * mm});
            skLineSegment(sketch, "E11.3.9.4", {"start": v(1492.25, 806.45) * mm, "end": v(1492.25, 787.4) * mm});
            skLineSegment(sketch, "E11.6.9.4", {"start": v(1511.3, 787.4) * mm, "end": v(1492.25, 787.4) * mm});
            skLineSegment(sketch, "E11.9.9.4", {"start": v(1511.3, 806.45) * mm, "end": v(1492.25, 806.45) * mm});
            skLineSegment(sketch, "E11.0.9.5", {"start": v(1511.3, 933.45) * mm, "end": v(1511.3, 914.4) * mm});
            skLineSegment(sketch, "E11.3.9.5", {"start": v(1492.25, 933.45) * mm, "end": v(1492.25, 914.4) * mm});
            skLineSegment(sketch, "E11.6.9.5", {"start": v(1511.3, 914.4) * mm, "end": v(1492.25, 914.4) * mm});
            skLineSegment(sketch, "E11.9.9.5", {"start": v(1511.3, 933.45) * mm, "end": v(1492.25, 933.45) * mm});
            skLineSegment(sketch, "E11.0.9.6", {"start": v(1511.3, 1060.45) * mm, "end": v(1511.3, 1041.4) * mm});
            skLineSegment(sketch, "E11.3.9.6", {"start": v(1492.25, 1060.45) * mm, "end": v(1492.25, 1041.4) * mm});
            skLineSegment(sketch, "E11.6.9.6", {"start": v(1511.3, 1041.4) * mm, "end": v(1492.25, 1041.4) * mm});
            skLineSegment(sketch, "E11.9.9.6", {"start": v(1511.3, 1060.45) * mm, "end": v(1492.25, 1060.45) * mm});
            skLineSegment(sketch, "E11.0.9.7", {"start": v(1511.3, 1187.45) * mm, "end": v(1511.3, 1168.4) * mm});
            skLineSegment(sketch, "E11.3.9.7", {"start": v(1492.25, 1187.45) * mm, "end": v(1492.25, 1168.4) * mm});
            skLineSegment(sketch, "E11.6.9.7", {"start": v(1511.3, 1168.4) * mm, "end": v(1492.25, 1168.4) * mm});
            skLineSegment(sketch, "E11.9.9.7", {"start": v(1511.3, 1187.45) * mm, "end": v(1492.25, 1187.45) * mm});
            skLineSegment(sketch, "E11.0.9.8", {"start": v(1511.3, 1314.45) * mm, "end": v(1511.3, 1295.4) * mm});
            skLineSegment(sketch, "E11.3.9.8", {"start": v(1492.25, 1314.45) * mm, "end": v(1492.25, 1295.4) * mm});
            skLineSegment(sketch, "E11.6.9.8", {"start": v(1511.3, 1295.4) * mm, "end": v(1492.25, 1295.4) * mm});
            skLineSegment(sketch, "E11.9.9.8", {"start": v(1511.3, 1314.45) * mm, "end": v(1492.25, 1314.45) * mm});
            skLineSegment(sketch, "E11.0.9.9", {"start": v(1511.3, 1441.45) * mm, "end": v(1511.3, 1422.4) * mm});
            skLineSegment(sketch, "E11.3.9.9", {"start": v(1492.25, 1441.45) * mm, "end": v(1492.25, 1422.4) * mm});
            skLineSegment(sketch, "E11.6.9.9", {"start": v(1511.3, 1422.4) * mm, "end": v(1492.25, 1422.4) * mm});
            skLineSegment(sketch, "E11.9.9.9", {"start": v(1511.3, 1441.45) * mm, "end": v(1492.25, 1441.45) * mm});
            skLineSegment(sketch, "E11.0.10.0", {"start": v(1657.35, 298.45) * mm, "end": v(1657.35, 279.4) * mm});
            skLineSegment(sketch, "E11.3.10.0", {"start": v(1638.3, 298.45) * mm, "end": v(1638.3, 279.4) * mm});
            skLineSegment(sketch, "E11.6.10.0", {"start": v(1657.35, 279.4) * mm, "end": v(1638.3, 279.4) * mm});
            skLineSegment(sketch, "E11.9.10.0", {"start": v(1657.35, 298.45) * mm, "end": v(1638.3, 298.45) * mm});
            skLineSegment(sketch, "E11.0.10.1", {"start": v(1657.35, 425.45) * mm, "end": v(1657.35, 406.4) * mm});
            skLineSegment(sketch, "E11.3.10.1", {"start": v(1638.3, 425.45) * mm, "end": v(1638.3, 406.4) * mm});
            skLineSegment(sketch, "E11.6.10.1", {"start": v(1657.35, 406.4) * mm, "end": v(1638.3, 406.4) * mm});
            skLineSegment(sketch, "E11.9.10.1", {"start": v(1657.35, 425.45) * mm, "end": v(1638.3, 425.45) * mm});
            skLineSegment(sketch, "E11.0.10.2", {"start": v(1657.35, 552.45) * mm, "end": v(1657.35, 533.4) * mm});
            skLineSegment(sketch, "E11.3.10.2", {"start": v(1638.3, 552.45) * mm, "end": v(1638.3, 533.4) * mm});
            skLineSegment(sketch, "E11.6.10.2", {"start": v(1657.35, 533.4) * mm, "end": v(1638.3, 533.4) * mm});
            skLineSegment(sketch, "E11.9.10.2", {"start": v(1657.35, 552.45) * mm, "end": v(1638.3, 552.45) * mm});
            skLineSegment(sketch, "E11.0.10.3", {"start": v(1657.35, 679.45) * mm, "end": v(1657.35, 660.4) * mm});
            skLineSegment(sketch, "E11.3.10.3", {"start": v(1638.3, 679.45) * mm, "end": v(1638.3, 660.4) * mm});
            skLineSegment(sketch, "E11.6.10.3", {"start": v(1657.35, 660.4) * mm, "end": v(1638.3, 660.4) * mm});
            skLineSegment(sketch, "E11.9.10.3", {"start": v(1657.35, 679.45) * mm, "end": v(1638.3, 679.45) * mm});
            skLineSegment(sketch, "E11.0.10.4", {"start": v(1657.35, 806.45) * mm, "end": v(1657.35, 787.4) * mm});
            skLineSegment(sketch, "E11.3.10.4", {"start": v(1638.3, 806.45) * mm, "end": v(1638.3, 787.4) * mm});
            skLineSegment(sketch, "E11.6.10.4", {"start": v(1657.35, 787.4) * mm, "end": v(1638.3, 787.4) * mm});
            skLineSegment(sketch, "E11.9.10.4", {"start": v(1657.35, 806.45) * mm, "end": v(1638.3, 806.45) * mm});
            skLineSegment(sketch, "E11.0.10.5", {"start": v(1657.35, 933.45) * mm, "end": v(1657.35, 914.4) * mm});
            skLineSegment(sketch, "E11.3.10.5", {"start": v(1638.3, 933.45) * mm, "end": v(1638.3, 914.4) * mm});
            skLineSegment(sketch, "E11.6.10.5", {"start": v(1657.35, 914.4) * mm, "end": v(1638.3, 914.4) * mm});
            skLineSegment(sketch, "E11.9.10.5", {"start": v(1657.35, 933.45) * mm, "end": v(1638.3, 933.45) * mm});
            skLineSegment(sketch, "E11.0.10.6", {"start": v(1657.35, 1060.45) * mm, "end": v(1657.35, 1041.4) * mm});
            skLineSegment(sketch, "E11.3.10.6", {"start": v(1638.3, 1060.45) * mm, "end": v(1638.3, 1041.4) * mm});
            skLineSegment(sketch, "E11.6.10.6", {"start": v(1657.35, 1041.4) * mm, "end": v(1638.3, 1041.4) * mm});
            skLineSegment(sketch, "E11.9.10.6", {"start": v(1657.35, 1060.45) * mm, "end": v(1638.3, 1060.45) * mm});
            skLineSegment(sketch, "E11.0.10.7", {"start": v(1657.35, 1187.45) * mm, "end": v(1657.35, 1168.4) * mm});
            skLineSegment(sketch, "E11.3.10.7", {"start": v(1638.3, 1187.45) * mm, "end": v(1638.3, 1168.4) * mm});
            skLineSegment(sketch, "E11.6.10.7", {"start": v(1657.35, 1168.4) * mm, "end": v(1638.3, 1168.4) * mm});
            skLineSegment(sketch, "E11.9.10.7", {"start": v(1657.35, 1187.45) * mm, "end": v(1638.3, 1187.45) * mm});
            skLineSegment(sketch, "E11.0.10.8", {"start": v(1657.35, 1314.45) * mm, "end": v(1657.35, 1295.4) * mm});
            skLineSegment(sketch, "E11.3.10.8", {"start": v(1638.3, 1314.45) * mm, "end": v(1638.3, 1295.4) * mm});
            skLineSegment(sketch, "E11.6.10.8", {"start": v(1657.35, 1295.4) * mm, "end": v(1638.3, 1295.4) * mm});
            skLineSegment(sketch, "E11.9.10.8", {"start": v(1657.35, 1314.45) * mm, "end": v(1638.3, 1314.45) * mm});
            skLineSegment(sketch, "E11.0.10.9", {"start": v(1657.35, 1441.45) * mm, "end": v(1657.35, 1422.4) * mm});
            skLineSegment(sketch, "E11.3.10.9", {"start": v(1638.3, 1441.45) * mm, "end": v(1638.3, 1422.4) * mm});
            skLineSegment(sketch, "E11.6.10.9", {"start": v(1657.35, 1422.4) * mm, "end": v(1638.3, 1422.4) * mm});
            skLineSegment(sketch, "E11.9.10.9", {"start": v(1657.35, 1441.45) * mm, "end": v(1638.3, 1441.45) * mm});
            skSolve(sketch);
        }
        {
            var Q0;
            Q0 = qSketchRegion(id + "F6", true);
            var Q1;
            {var subQ0=sQuery(id+"F0.wireOp",EDGE,"E3.right");var subQ1=sQuery(id+"F0.wireOp",EDGE,"E3.left");var subQ2=sQuery(id+"F0.wireOp",EDGE,"E3.top");var subQ3=sQuery(id+"F0.wireOp",EDGE,"E3.bottom");var subQ4=sQuery(id+"F0.wireOp",EDGE,"E2.top");var subQ5=sQuery(id+"F0.wireOp",EDGE,"E2.bottom");var subQ6=sQuery(id+"F0.wireOp",EDGE,"E1.top");var subQ7=sQuery(id+"F0.wireOp",EDGE,"E1.bottom");var subQ8=sQuery(id+"F0.wireOp",EDGE,"E0.right");var subQ9=sQuery(id+"F0.wireOp",EDGE,"E0.left");var subQ10=sQuery(id+"F0.wireOp",EDGE,"E0.top");var subQ11=sQuery(id+"F0.wireOp",EDGE,"E0.bottom");Q1=makeQuery(id+"F3.boolean.opBoolean","MERGE",FACE,{"derivedFrom":[makeQuery(id+"F1.opExtrude","CAP_FACE",FACE,{"disambiguationData":[OSD([subQ11,subQ10,subQ9,subQ8,subQ7,subQ6,subQ5,subQ4,subQ3,subQ2,subQ1,subQ0])],"isStart":false}),makeQuery(id+"F3.opExtrude","CAP_FACE",FACE,{"disambiguationData":[OSD([subQ11,subQ10,subQ9,subQ8,subQ7,subQ6,subQ5,subQ4,subQ3,subQ2,subQ1,subQ0,sQuery(id+"F2.wireOp",EDGE,"E4.left"),sQuery(id+"F2.wireOp",EDGE,"E4.right"),sQuery(id+"F2.wireOp",EDGE,"E5.1.0.0"),sQuery(id+"F2.wireOp",EDGE,"E5.1.0.1"),sQuery(id+"F2.wireOp",EDGE,"E5.2.0.0"),sQuery(id+"F2.wireOp",EDGE,"E5.2.0.1"),sQuery(id+"F2.wireOp",EDGE,"E5.3.0.0"),sQuery(id+"F2.wireOp",EDGE,"E5.3.0.1"),sQuery(id+"F2.wireOp",EDGE,"E5.4.0.0"),sQuery(id+"F2.wireOp",EDGE,"E5.4.0.1"),sQuery(id+"F2.wireOp",EDGE,"E5.5.0.0"),sQuery(id+"F2.wireOp",EDGE,"E5.5.0.1"),sQuery(id+"F2.wireOp",EDGE,"E5.6.0.0"),sQuery(id+"F2.wireOp",EDGE,"E5.6.0.1"),sQuery(id+"F2.wireOp",EDGE,"E5.7.0.0"),sQuery(id+"F2.wireOp",EDGE,"E5.7.0.1"),sQuery(id+"F2.wireOp",EDGE,"E5.8.0.0"),sQuery(id+"F2.wireOp",EDGE,"E5.8.0.1"),sQuery(id+"F2.wireOp",EDGE,"E5.9.0.0"),sQuery(id+"F2.wireOp",EDGE,"E5.9.0.1"),sQuery(id+"F2.wireOp",EDGE,"E5.10.0.0")])],"isStart":true})]});}
            var Q2;
            {var subQ0=sQuery(id+"F0.wireOp",EDGE,"E3.right");var subQ1=sQuery(id+"F0.wireOp",EDGE,"E3.left");var subQ2=sQuery(id+"F0.wireOp",EDGE,"E3.top");var subQ3=sQuery(id+"F0.wireOp",EDGE,"E3.bottom");var subQ4=sQuery(id+"F0.wireOp",EDGE,"E2.top");var subQ5=sQuery(id+"F0.wireOp",EDGE,"E2.bottom");var subQ6=sQuery(id+"F0.wireOp",EDGE,"E1.top");var subQ7=sQuery(id+"F0.wireOp",EDGE,"E1.bottom");var subQ8=sQuery(id+"F0.wireOp",EDGE,"E0.right");var subQ9=sQuery(id+"F0.wireOp",EDGE,"E0.left");var subQ10=sQuery(id+"F0.wireOp",EDGE,"E0.top");var subQ11=sQuery(id+"F0.wireOp",EDGE,"E0.bottom");Q2=makeQuery(id+"F5.opPattern","COPY",FACE,{"derivedFrom":makeQuery(id+"F3.boolean.opBoolean","MERGE",FACE,{"derivedFrom":[makeQuery(id+"F1.opExtrude","CAP_FACE",FACE,{"disambiguationData":[OSD([subQ11,subQ10,subQ9,subQ8,subQ7,subQ6,subQ5,subQ4,subQ3,subQ2,subQ1,subQ0])],"isStart":false}),makeQuery(id+"F3.opExtrude","CAP_FACE",FACE,{"disambiguationData":[OSD([subQ11,subQ10,subQ9,subQ8,subQ7,subQ6,subQ5,subQ4,subQ3,subQ2,subQ1,subQ0,sQuery(id+"F2.wireOp",EDGE,"E4.left"),sQuery(id+"F2.wireOp",EDGE,"E4.right"),sQuery(id+"F2.wireOp",EDGE,"E5.1.0.0"),sQuery(id+"F2.wireOp",EDGE,"E5.1.0.1"),sQuery(id+"F2.wireOp",EDGE,"E5.2.0.0"),sQuery(id+"F2.wireOp",EDGE,"E5.2.0.1"),sQuery(id+"F2.wireOp",EDGE,"E5.3.0.0"),sQuery(id+"F2.wireOp",EDGE,"E5.3.0.1"),sQuery(id+"F2.wireOp",EDGE,"E5.4.0.0"),sQuery(id+"F2.wireOp",EDGE,"E5.4.0.1"),sQuery(id+"F2.wireOp",EDGE,"E5.5.0.0"),sQuery(id+"F2.wireOp",EDGE,"E5.5.0.1"),sQuery(id+"F2.wireOp",EDGE,"E5.6.0.0"),sQuery(id+"F2.wireOp",EDGE,"E5.6.0.1"),sQuery(id+"F2.wireOp",EDGE,"E5.7.0.0"),sQuery(id+"F2.wireOp",EDGE,"E5.7.0.1"),sQuery(id+"F2.wireOp",EDGE,"E5.8.0.0"),sQuery(id+"F2.wireOp",EDGE,"E5.8.0.1"),sQuery(id+"F2.wireOp",EDGE,"E5.9.0.0"),sQuery(id+"F2.wireOp",EDGE,"E5.9.0.1"),sQuery(id+"F2.wireOp",EDGE,"E5.10.0.0")])],"isStart":true})]}),"instanceName":"1"});}
            extrude(context, id + "F7", {"entities" : qUnion([Q0]), "operationType" : NewBodyOperationType.ADD, "endBound" : BoundingType.UP_TO_SURFACE, "endBoundEntityFace" : qUnion([Q1]), "depth" : 25.4 * mm, "hasSecondDirection" : true, "secondDirectionBound" : SecondDirectionBoundingType.UP_TO_SURFACE, "secondDirectionOppositeDirection" : true, "secondDirectionBoundEntityFace" : qUnion([Q2]), "secondDirectionDepth" : 25.4 * mm});
        }
    });
